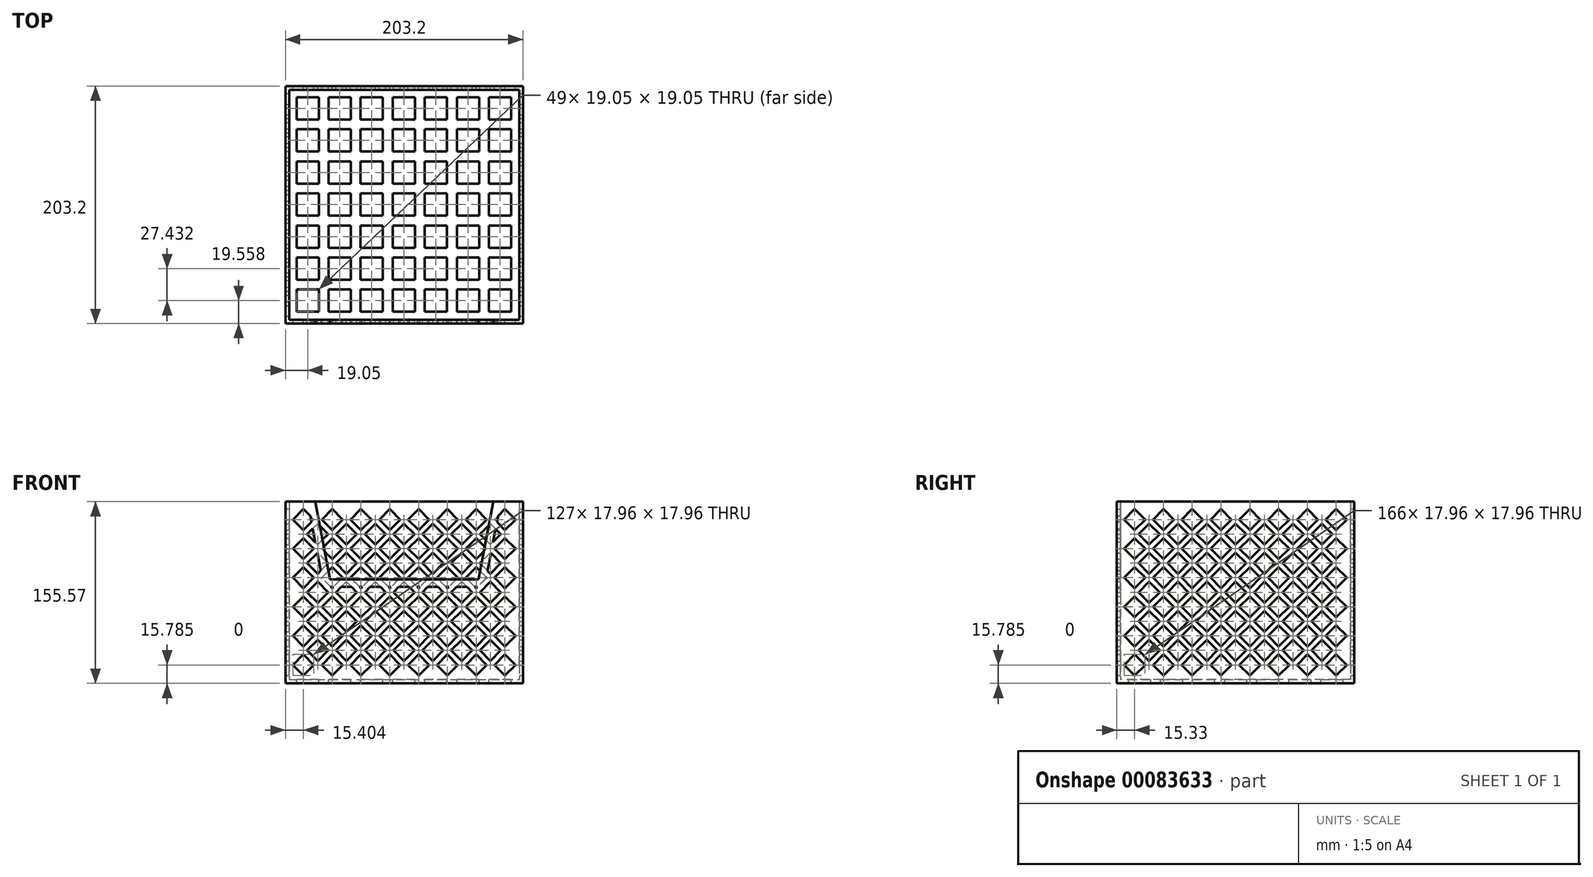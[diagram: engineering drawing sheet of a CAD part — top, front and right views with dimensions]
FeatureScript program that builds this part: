
annotation { "Feature Type Name" : "Feature", "Feature Type Description" : "" }
export const myFeature = defineFeature(function(context is Context, id is Id, definition is map)
    precondition{}
    {
        {
            var Q0;
            Q0=qCreatedBy(makeId("Top.planeOp"),FACE);
            var sketch = newSketch(context, id + "F0", { "sketchPlane" : qUnion([Q0])});
            skLineSegment(sketch, "E0.bottom", {"start": v(-101.6, 101.6) * mm, "end": v(101.6, 101.6) * mm});
            skLineSegment(sketch, "E0.top", {"start": v(-101.6, -101.6) * mm, "end": v(101.6, -101.6) * mm});
            skLineSegment(sketch, "E0.left", {"start": v(-101.6, 101.6) * mm, "end": v(-101.6, -101.6) * mm});
            skLineSegment(sketch, "E0.right", {"start": v(101.6, 101.6) * mm, "end": v(101.6, -101.6) * mm});
            skPoint(sketch, "E0.middle", {"position": v(0, 0) * mm});
            skSolve(sketch);
        }
        {
            var Q0;
            Q0=qSketchRegion(id+"F0",true);
            extrude(context, id + "F1", {"entities" : qUnion([Q0]), "depth" : 3.17 * mm});
        }
        {
            var Q0;
            Q0=makeQuery(id+"F1.opExtrude","CAP_FACE",FACE,{"disambiguationData":[OSD([sQuery(id+"F0.wireOp",EDGE,"E0.bottom"),sQuery(id+"F0.wireOp",EDGE,"E0.top"),sQuery(id+"F0.wireOp",EDGE,"E0.left"),sQuery(id+"F0.wireOp",EDGE,"E0.right")])],"isStart":false});
            var sketch = newSketch(context, id + "F2", { "sketchPlane" : qUnion([Q0])});
            skLineSegment(sketch, "E1.bottom", {"start": v(-101.6, 101.6) * mm, "end": v(101.6, 101.6) * mm});
            skLineSegment(sketch, "E1.top", {"start": v(-101.6, -101.6) * mm, "end": v(101.6, -101.6) * mm});
            skLineSegment(sketch, "E1.left", {"start": v(-101.6, 101.6) * mm, "end": v(-101.6, -101.6) * mm});
            skLineSegment(sketch, "E1.right", {"start": v(101.6, 101.6) * mm, "end": v(101.6, -101.6) * mm});
            skPoint(sketch, "E1.middle", {"position": v(0, 0) * mm});
            skLineSegment(sketch, "E2.bottom", {"start": v(-98.42, 98.43) * mm, "end": v(98.42, 98.43) * mm});
            skLineSegment(sketch, "E2.top", {"start": v(-98.42, -98.43) * mm, "end": v(98.42, -98.43) * mm});
            skLineSegment(sketch, "E2.left", {"start": v(-98.42, 98.43) * mm, "end": v(-98.42, -98.43) * mm});
            skLineSegment(sketch, "E2.right", {"start": v(98.42, 98.43) * mm, "end": v(98.42, -98.43) * mm});
            skSolve(sketch);
        }
        {
            var Q0;
            Q0=qSketchRegion(id+"F2",true);
            extrude(context, id + "F3", {"entities" : qUnion([Q0]), "operationType" : NewBodyOperationType.ADD, "depth" : 152.4 * mm});
        }
        {
            var Q0;
            Q0=makeQuery(id+"F3.boolean.opBoolean","MERGE",FACE,{"derivedFrom":[makeQuery(id+"F1.opExtrude","SWEPT_FACE",FACE,{"disambiguationData":[OSD([sQuery(id+"F0.wireOp",EDGE,"E0.top")])]}),makeQuery(id+"F3.opExtrude","SWEPT_FACE",FACE,{"disambiguationData":[OSD([sQuery(id+"F2.wireOp",EDGE,"E1.top")])]})]});
            var sketch = newSketch(context, id + "F4", { "sketchPlane" : qUnion([Q0])});
            skLineSegment(sketch, "E3", {"start": v(0, 155.58) * mm, "end": v(0, 88.9) * mm, "construction": true});
            skLineSegment(sketch, "E4", {"start": v(0, 88.9) * mm, "end": v(-63.5, 88.9) * mm});
            skLineSegment(sketch, "E5", {"start": v(-63.5, 88.9) * mm, "end": v(-76.2, 155.58) * mm});
            skLineSegment(sketch, "E6", {"start": v(-76.2, 155.58) * mm, "end": v(0, 155.58) * mm});
            skLineSegment(sketch, "E7.MirrorCS", {"start": v(0, 88.9) * mm, "end": v(63.5, 88.9) * mm});
            skLineSegment(sketch, "E8.MirrorCS", {"start": v(76.2, 155.58) * mm, "end": v(0, 155.58) * mm});
            skLineSegment(sketch, "E9.MirrorCS", {"start": v(63.5, 88.9) * mm, "end": v(76.2, 155.58) * mm});
            skSolve(sketch);
        }
        {
            var Q0;
            Q0=qSketchRegion(id+"F4",true);
            extrude(context, id + "F5", {"entities" : qUnion([Q0]), "operationType" : NewBodyOperationType.REMOVE, "endBound" : BoundingType.UP_TO_NEXT, "oppositeDirection" : true, "depth" : 25.4 * mm});
        }
        {
            var Q0;
            Q0=makeQuery(id+"F3.boolean.opBoolean","MERGE",FACE,{"derivedFrom":[makeQuery(id+"F1.opExtrude","SWEPT_FACE",FACE,{"disambiguationData":[OSD([sQuery(id+"F0.wireOp",EDGE,"E0.right")])]}),makeQuery(id+"F3.opExtrude","SWEPT_FACE",FACE,{"disambiguationData":[OSD([sQuery(id+"F2.wireOp",EDGE,"E1.right")])]})]});
            var sketch = newSketch(context, id + "F6", { "sketchPlane" : qUnion([Q0])});
            skLineSegment(sketch, "E10", {"start": v(-86.27, 149.23) * mm, "end": v(-95.25, 140.24) * mm});
            skLineSegment(sketch, "E11", {"start": v(-95.25, 140.24) * mm, "end": v(-86.27, 131.26) * mm});
            skLineSegment(sketch, "E12", {"start": v(-86.27, 131.26) * mm, "end": v(-77.29, 140.24) * mm});
            skLineSegment(sketch, "E13", {"start": v(-77.29, 140.24) * mm, "end": v(-86.27, 149.23) * mm});
            skLineSegment(sketch, "E14", {"start": v(-86.27, 131.26) * mm, "end": v(-63.2, 131.26) * mm, "construction": true});
            skLineSegment(sketch, "E15.0.1.0", {"start": v(-95.25, 115.35) * mm, "end": v(-86.27, 106.37) * mm});
            skLineSegment(sketch, "E15.0.1.1", {"start": v(-86.27, 106.37) * mm, "end": v(-77.29, 115.35) * mm});
            skLineSegment(sketch, "E15.0.1.2", {"start": v(-77.29, 115.35) * mm, "end": v(-86.27, 124.33) * mm});
            skLineSegment(sketch, "E15.0.1.3", {"start": v(-86.27, 124.33) * mm, "end": v(-95.25, 115.35) * mm});
            skLineSegment(sketch, "E15.0.2.0", {"start": v(-95.25, 90.46) * mm, "end": v(-86.27, 81.48) * mm});
            skLineSegment(sketch, "E15.0.2.1", {"start": v(-86.27, 81.48) * mm, "end": v(-77.29, 90.46) * mm});
            skLineSegment(sketch, "E15.0.2.2", {"start": v(-77.29, 90.46) * mm, "end": v(-86.27, 99.44) * mm});
            skLineSegment(sketch, "E15.0.2.3", {"start": v(-86.27, 99.44) * mm, "end": v(-95.25, 90.46) * mm});
            skLineSegment(sketch, "E15.0.3.0", {"start": v(-95.25, 65.57) * mm, "end": v(-86.27, 56.59) * mm});
            skLineSegment(sketch, "E15.0.3.1", {"start": v(-86.27, 56.59) * mm, "end": v(-77.29, 65.57) * mm});
            skLineSegment(sketch, "E15.0.3.2", {"start": v(-77.29, 65.57) * mm, "end": v(-86.27, 74.55) * mm});
            skLineSegment(sketch, "E15.0.3.3", {"start": v(-86.27, 74.55) * mm, "end": v(-95.25, 65.57) * mm});
            skLineSegment(sketch, "E15.0.4.0", {"start": v(-95.25, 40.68) * mm, "end": v(-86.27, 31.7) * mm});
            skLineSegment(sketch, "E15.0.4.1", {"start": v(-86.27, 31.7) * mm, "end": v(-77.29, 40.68) * mm});
            skLineSegment(sketch, "E15.0.4.2", {"start": v(-77.29, 40.68) * mm, "end": v(-86.27, 49.66) * mm});
            skLineSegment(sketch, "E15.0.4.3", {"start": v(-86.27, 49.66) * mm, "end": v(-95.25, 40.68) * mm});
            skLineSegment(sketch, "E15.0.5.0", {"start": v(-95.25, 15.78) * mm, "end": v(-86.27, 6.8) * mm});
            skLineSegment(sketch, "E15.0.5.1", {"start": v(-86.27, 6.8) * mm, "end": v(-77.29, 15.78) * mm});
            skLineSegment(sketch, "E15.0.5.2", {"start": v(-77.29, 15.78) * mm, "end": v(-86.27, 24.77) * mm});
            skLineSegment(sketch, "E15.0.5.3", {"start": v(-86.27, 24.77) * mm, "end": v(-95.25, 15.78) * mm});
            skLineSegment(sketch, "E15.1.0.0", {"start": v(-70.61, 140.24) * mm, "end": v(-61.63, 131.26) * mm});
            skLineSegment(sketch, "E15.1.0.1", {"start": v(-61.63, 131.26) * mm, "end": v(-52.65, 140.24) * mm});
            skLineSegment(sketch, "E15.1.0.2", {"start": v(-52.65, 140.24) * mm, "end": v(-61.63, 149.23) * mm});
            skLineSegment(sketch, "E15.1.0.3", {"start": v(-61.63, 149.23) * mm, "end": v(-70.61, 140.24) * mm});
            skLineSegment(sketch, "E15.1.1.0", {"start": v(-70.61, 115.35) * mm, "end": v(-61.63, 106.37) * mm});
            skLineSegment(sketch, "E15.1.1.1", {"start": v(-61.63, 106.37) * mm, "end": v(-52.65, 115.35) * mm});
            skLineSegment(sketch, "E15.1.1.2", {"start": v(-52.65, 115.35) * mm, "end": v(-61.63, 124.33) * mm});
            skLineSegment(sketch, "E15.1.1.3", {"start": v(-61.63, 124.33) * mm, "end": v(-70.61, 115.35) * mm});
            skLineSegment(sketch, "E15.1.2.0", {"start": v(-70.61, 90.46) * mm, "end": v(-61.63, 81.48) * mm});
            skLineSegment(sketch, "E15.1.2.1", {"start": v(-61.63, 81.48) * mm, "end": v(-52.65, 90.46) * mm});
            skLineSegment(sketch, "E15.1.2.2", {"start": v(-52.65, 90.46) * mm, "end": v(-61.63, 99.44) * mm});
            skLineSegment(sketch, "E15.1.2.3", {"start": v(-61.63, 99.44) * mm, "end": v(-70.61, 90.46) * mm});
            skLineSegment(sketch, "E15.1.3.0", {"start": v(-70.61, 65.57) * mm, "end": v(-61.63, 56.59) * mm});
            skLineSegment(sketch, "E15.1.3.1", {"start": v(-61.63, 56.59) * mm, "end": v(-52.65, 65.57) * mm});
            skLineSegment(sketch, "E15.1.3.2", {"start": v(-52.65, 65.57) * mm, "end": v(-61.63, 74.55) * mm});
            skLineSegment(sketch, "E15.1.3.3", {"start": v(-61.63, 74.55) * mm, "end": v(-70.61, 65.57) * mm});
            skLineSegment(sketch, "E15.1.4.0", {"start": v(-70.61, 40.68) * mm, "end": v(-61.63, 31.7) * mm});
            skLineSegment(sketch, "E15.1.4.1", {"start": v(-61.63, 31.7) * mm, "end": v(-52.65, 40.68) * mm});
            skLineSegment(sketch, "E15.1.4.2", {"start": v(-52.65, 40.68) * mm, "end": v(-61.63, 49.66) * mm});
            skLineSegment(sketch, "E15.1.4.3", {"start": v(-61.63, 49.66) * mm, "end": v(-70.61, 40.68) * mm});
            skLineSegment(sketch, "E15.1.5.0", {"start": v(-70.61, 15.78) * mm, "end": v(-61.63, 6.8) * mm});
            skLineSegment(sketch, "E15.1.5.1", {"start": v(-61.63, 6.8) * mm, "end": v(-52.65, 15.78) * mm});
            skLineSegment(sketch, "E15.1.5.2", {"start": v(-52.65, 15.78) * mm, "end": v(-61.63, 24.77) * mm});
            skLineSegment(sketch, "E15.1.5.3", {"start": v(-61.63, 24.77) * mm, "end": v(-70.61, 15.78) * mm});
            skLineSegment(sketch, "E15.2.0.0", {"start": v(-45.97, 140.24) * mm, "end": v(-37, 131.26) * mm});
            skLineSegment(sketch, "E15.2.0.1", {"start": v(-37, 131.26) * mm, "end": v(-28.01, 140.24) * mm});
            skLineSegment(sketch, "E15.2.0.2", {"start": v(-28.01, 140.24) * mm, "end": v(-37, 149.23) * mm});
            skLineSegment(sketch, "E15.2.0.3", {"start": v(-37, 149.23) * mm, "end": v(-45.97, 140.24) * mm});
            skLineSegment(sketch, "E15.2.1.0", {"start": v(-45.97, 115.35) * mm, "end": v(-37, 106.37) * mm});
            skLineSegment(sketch, "E15.2.1.1", {"start": v(-37, 106.37) * mm, "end": v(-28.01, 115.35) * mm});
            skLineSegment(sketch, "E15.2.1.2", {"start": v(-28.01, 115.35) * mm, "end": v(-37, 124.33) * mm});
            skLineSegment(sketch, "E15.2.1.3", {"start": v(-37, 124.33) * mm, "end": v(-45.97, 115.35) * mm});
            skLineSegment(sketch, "E15.2.2.0", {"start": v(-45.97, 90.46) * mm, "end": v(-37, 81.48) * mm});
            skLineSegment(sketch, "E15.2.2.1", {"start": v(-37, 81.48) * mm, "end": v(-28.01, 90.46) * mm});
            skLineSegment(sketch, "E15.2.2.2", {"start": v(-28.01, 90.46) * mm, "end": v(-37, 99.44) * mm});
            skLineSegment(sketch, "E15.2.2.3", {"start": v(-37, 99.44) * mm, "end": v(-45.97, 90.46) * mm});
            skLineSegment(sketch, "E15.2.3.0", {"start": v(-45.97, 65.57) * mm, "end": v(-37, 56.59) * mm});
            skLineSegment(sketch, "E15.2.3.1", {"start": v(-37, 56.59) * mm, "end": v(-28.01, 65.57) * mm});
            skLineSegment(sketch, "E15.2.3.2", {"start": v(-28.01, 65.57) * mm, "end": v(-37, 74.55) * mm});
            skLineSegment(sketch, "E15.2.3.3", {"start": v(-37, 74.55) * mm, "end": v(-45.97, 65.57) * mm});
            skLineSegment(sketch, "E15.2.4.0", {"start": v(-45.97, 40.68) * mm, "end": v(-37, 31.7) * mm});
            skLineSegment(sketch, "E15.2.4.1", {"start": v(-37, 31.7) * mm, "end": v(-28.01, 40.68) * mm});
            skLineSegment(sketch, "E15.2.4.2", {"start": v(-28.01, 40.68) * mm, "end": v(-37, 49.66) * mm});
            skLineSegment(sketch, "E15.2.4.3", {"start": v(-37, 49.66) * mm, "end": v(-45.97, 40.68) * mm});
            skLineSegment(sketch, "E15.2.5.0", {"start": v(-45.97, 15.78) * mm, "end": v(-37, 6.8) * mm});
            skLineSegment(sketch, "E15.2.5.1", {"start": v(-37, 6.8) * mm, "end": v(-28.01, 15.78) * mm});
            skLineSegment(sketch, "E15.2.5.2", {"start": v(-28.01, 15.78) * mm, "end": v(-37, 24.77) * mm});
            skLineSegment(sketch, "E15.2.5.3", {"start": v(-37, 24.77) * mm, "end": v(-45.97, 15.78) * mm});
            skLineSegment(sketch, "E15.3.0.0", {"start": v(-21.34, 140.24) * mm, "end": v(-12.36, 131.26) * mm});
            skLineSegment(sketch, "E15.3.0.1", {"start": v(-12.36, 131.26) * mm, "end": v(-3.38, 140.24) * mm});
            skLineSegment(sketch, "E15.3.0.2", {"start": v(-3.38, 140.24) * mm, "end": v(-12.36, 149.23) * mm});
            skLineSegment(sketch, "E15.3.0.3", {"start": v(-12.36, 149.23) * mm, "end": v(-21.34, 140.24) * mm});
            skLineSegment(sketch, "E15.3.1.0", {"start": v(-21.34, 115.35) * mm, "end": v(-12.36, 106.37) * mm});
            skLineSegment(sketch, "E15.3.1.1", {"start": v(-12.36, 106.37) * mm, "end": v(-3.38, 115.35) * mm});
            skLineSegment(sketch, "E15.3.1.2", {"start": v(-3.38, 115.35) * mm, "end": v(-12.36, 124.33) * mm});
            skLineSegment(sketch, "E15.3.1.3", {"start": v(-12.36, 124.33) * mm, "end": v(-21.34, 115.35) * mm});
            skLineSegment(sketch, "E15.3.2.0", {"start": v(-21.34, 90.46) * mm, "end": v(-12.36, 81.48) * mm});
            skLineSegment(sketch, "E15.3.2.1", {"start": v(-12.36, 81.48) * mm, "end": v(-3.38, 90.46) * mm});
            skLineSegment(sketch, "E15.3.2.2", {"start": v(-3.38, 90.46) * mm, "end": v(-12.36, 99.44) * mm});
            skLineSegment(sketch, "E15.3.2.3", {"start": v(-12.36, 99.44) * mm, "end": v(-21.34, 90.46) * mm});
            skLineSegment(sketch, "E15.3.3.0", {"start": v(-21.34, 65.57) * mm, "end": v(-12.36, 56.59) * mm});
            skLineSegment(sketch, "E15.3.3.1", {"start": v(-12.36, 56.59) * mm, "end": v(-3.38, 65.57) * mm});
            skLineSegment(sketch, "E15.3.3.2", {"start": v(-3.38, 65.57) * mm, "end": v(-12.36, 74.55) * mm});
            skLineSegment(sketch, "E15.3.3.3", {"start": v(-12.36, 74.55) * mm, "end": v(-21.34, 65.57) * mm});
            skLineSegment(sketch, "E15.3.4.0", {"start": v(-21.34, 40.68) * mm, "end": v(-12.36, 31.7) * mm});
            skLineSegment(sketch, "E15.3.4.1", {"start": v(-12.36, 31.7) * mm, "end": v(-3.38, 40.68) * mm});
            skLineSegment(sketch, "E15.3.4.2", {"start": v(-3.38, 40.68) * mm, "end": v(-12.36, 49.66) * mm});
            skLineSegment(sketch, "E15.3.4.3", {"start": v(-12.36, 49.66) * mm, "end": v(-21.34, 40.68) * mm});
            skLineSegment(sketch, "E15.3.5.0", {"start": v(-21.34, 15.78) * mm, "end": v(-12.36, 6.8) * mm});
            skLineSegment(sketch, "E15.3.5.1", {"start": v(-12.36, 6.8) * mm, "end": v(-3.38, 15.78) * mm});
            skLineSegment(sketch, "E15.3.5.2", {"start": v(-3.38, 15.78) * mm, "end": v(-12.36, 24.77) * mm});
            skLineSegment(sketch, "E15.3.5.3", {"start": v(-12.36, 24.77) * mm, "end": v(-21.34, 15.78) * mm});
            skLineSegment(sketch, "E15.4.0.0", {"start": v(3.3, 140.24) * mm, "end": v(12.28, 131.26) * mm});
            skLineSegment(sketch, "E15.4.0.1", {"start": v(12.28, 131.26) * mm, "end": v(21.26, 140.24) * mm});
            skLineSegment(sketch, "E15.4.0.2", {"start": v(21.26, 140.24) * mm, "end": v(12.28, 149.23) * mm});
            skLineSegment(sketch, "E15.4.0.3", {"start": v(12.28, 149.23) * mm, "end": v(3.3, 140.24) * mm});
            skLineSegment(sketch, "E15.4.1.0", {"start": v(3.3, 115.35) * mm, "end": v(12.28, 106.37) * mm});
            skLineSegment(sketch, "E15.4.1.1", {"start": v(12.28, 106.37) * mm, "end": v(21.26, 115.35) * mm});
            skLineSegment(sketch, "E15.4.1.2", {"start": v(21.26, 115.35) * mm, "end": v(12.28, 124.33) * mm});
            skLineSegment(sketch, "E15.4.1.3", {"start": v(12.28, 124.33) * mm, "end": v(3.3, 115.35) * mm});
            skLineSegment(sketch, "E15.4.2.0", {"start": v(3.3, 90.46) * mm, "end": v(12.28, 81.48) * mm});
            skLineSegment(sketch, "E15.4.2.1", {"start": v(12.28, 81.48) * mm, "end": v(21.26, 90.46) * mm});
            skLineSegment(sketch, "E15.4.2.2", {"start": v(21.26, 90.46) * mm, "end": v(12.28, 99.44) * mm});
            skLineSegment(sketch, "E15.4.2.3", {"start": v(12.28, 99.44) * mm, "end": v(3.3, 90.46) * mm});
            skLineSegment(sketch, "E15.4.3.0", {"start": v(3.3, 65.57) * mm, "end": v(12.28, 56.59) * mm});
            skLineSegment(sketch, "E15.4.3.1", {"start": v(12.28, 56.59) * mm, "end": v(21.26, 65.57) * mm});
            skLineSegment(sketch, "E15.4.3.2", {"start": v(21.26, 65.57) * mm, "end": v(12.28, 74.55) * mm});
            skLineSegment(sketch, "E15.4.3.3", {"start": v(12.28, 74.55) * mm, "end": v(3.3, 65.57) * mm});
            skLineSegment(sketch, "E15.4.4.0", {"start": v(3.3, 40.68) * mm, "end": v(12.28, 31.7) * mm});
            skLineSegment(sketch, "E15.4.4.1", {"start": v(12.28, 31.7) * mm, "end": v(21.26, 40.68) * mm});
            skLineSegment(sketch, "E15.4.4.2", {"start": v(21.26, 40.68) * mm, "end": v(12.28, 49.66) * mm});
            skLineSegment(sketch, "E15.4.4.3", {"start": v(12.28, 49.66) * mm, "end": v(3.3, 40.68) * mm});
            skLineSegment(sketch, "E15.4.5.0", {"start": v(3.3, 15.78) * mm, "end": v(12.28, 6.8) * mm});
            skLineSegment(sketch, "E15.4.5.1", {"start": v(12.28, 6.8) * mm, "end": v(21.26, 15.78) * mm});
            skLineSegment(sketch, "E15.4.5.2", {"start": v(21.26, 15.78) * mm, "end": v(12.28, 24.77) * mm});
            skLineSegment(sketch, "E15.4.5.3", {"start": v(12.28, 24.77) * mm, "end": v(3.3, 15.78) * mm});
            skLineSegment(sketch, "E15.5.0.0", {"start": v(27.94, 140.24) * mm, "end": v(36.92, 131.26) * mm});
            skLineSegment(sketch, "E15.5.0.1", {"start": v(36.92, 131.26) * mm, "end": v(45.9, 140.24) * mm});
            skLineSegment(sketch, "E15.5.0.2", {"start": v(45.9, 140.24) * mm, "end": v(36.92, 149.23) * mm});
            skLineSegment(sketch, "E15.5.0.3", {"start": v(36.92, 149.23) * mm, "end": v(27.94, 140.24) * mm});
            skLineSegment(sketch, "E15.5.1.0", {"start": v(27.94, 115.35) * mm, "end": v(36.92, 106.37) * mm});
            skLineSegment(sketch, "E15.5.1.1", {"start": v(36.92, 106.37) * mm, "end": v(45.9, 115.35) * mm});
            skLineSegment(sketch, "E15.5.1.2", {"start": v(45.9, 115.35) * mm, "end": v(36.92, 124.33) * mm});
            skLineSegment(sketch, "E15.5.1.3", {"start": v(36.92, 124.33) * mm, "end": v(27.94, 115.35) * mm});
            skLineSegment(sketch, "E15.5.2.0", {"start": v(27.94, 90.46) * mm, "end": v(36.92, 81.48) * mm});
            skLineSegment(sketch, "E15.5.2.1", {"start": v(36.92, 81.48) * mm, "end": v(45.9, 90.46) * mm});
            skLineSegment(sketch, "E15.5.2.2", {"start": v(45.9, 90.46) * mm, "end": v(36.92, 99.44) * mm});
            skLineSegment(sketch, "E15.5.2.3", {"start": v(36.92, 99.44) * mm, "end": v(27.94, 90.46) * mm});
            skLineSegment(sketch, "E15.5.3.0", {"start": v(27.94, 65.57) * mm, "end": v(36.92, 56.59) * mm});
            skLineSegment(sketch, "E15.5.3.1", {"start": v(36.92, 56.59) * mm, "end": v(45.9, 65.57) * mm});
            skLineSegment(sketch, "E15.5.3.2", {"start": v(45.9, 65.57) * mm, "end": v(36.92, 74.55) * mm});
            skLineSegment(sketch, "E15.5.3.3", {"start": v(36.92, 74.55) * mm, "end": v(27.94, 65.57) * mm});
            skLineSegment(sketch, "E15.5.4.0", {"start": v(27.94, 40.68) * mm, "end": v(36.92, 31.7) * mm});
            skLineSegment(sketch, "E15.5.4.1", {"start": v(36.92, 31.7) * mm, "end": v(45.9, 40.68) * mm});
            skLineSegment(sketch, "E15.5.4.2", {"start": v(45.9, 40.68) * mm, "end": v(36.92, 49.66) * mm});
            skLineSegment(sketch, "E15.5.4.3", {"start": v(36.92, 49.66) * mm, "end": v(27.94, 40.68) * mm});
            skLineSegment(sketch, "E15.5.5.0", {"start": v(27.94, 15.78) * mm, "end": v(36.92, 6.8) * mm});
            skLineSegment(sketch, "E15.5.5.1", {"start": v(36.92, 6.8) * mm, "end": v(45.9, 15.78) * mm});
            skLineSegment(sketch, "E15.5.5.2", {"start": v(45.9, 15.78) * mm, "end": v(36.92, 24.77) * mm});
            skLineSegment(sketch, "E15.5.5.3", {"start": v(36.92, 24.77) * mm, "end": v(27.94, 15.78) * mm});
            skLineSegment(sketch, "E15.6.0.0", {"start": v(52.58, 140.24) * mm, "end": v(61.56, 131.26) * mm});
            skLineSegment(sketch, "E15.6.0.1", {"start": v(61.56, 131.26) * mm, "end": v(70.54, 140.24) * mm});
            skLineSegment(sketch, "E15.6.0.2", {"start": v(70.54, 140.24) * mm, "end": v(61.56, 149.23) * mm});
            skLineSegment(sketch, "E15.6.0.3", {"start": v(61.56, 149.23) * mm, "end": v(52.58, 140.24) * mm});
            skLineSegment(sketch, "E15.6.1.0", {"start": v(52.58, 115.35) * mm, "end": v(61.56, 106.37) * mm});
            skLineSegment(sketch, "E15.6.1.1", {"start": v(61.56, 106.37) * mm, "end": v(70.54, 115.35) * mm});
            skLineSegment(sketch, "E15.6.1.2", {"start": v(70.54, 115.35) * mm, "end": v(61.56, 124.33) * mm});
            skLineSegment(sketch, "E15.6.1.3", {"start": v(61.56, 124.33) * mm, "end": v(52.58, 115.35) * mm});
            skLineSegment(sketch, "E15.6.2.0", {"start": v(52.58, 90.46) * mm, "end": v(61.56, 81.48) * mm});
            skLineSegment(sketch, "E15.6.2.1", {"start": v(61.56, 81.48) * mm, "end": v(70.54, 90.46) * mm});
            skLineSegment(sketch, "E15.6.2.2", {"start": v(70.54, 90.46) * mm, "end": v(61.56, 99.44) * mm});
            skLineSegment(sketch, "E15.6.2.3", {"start": v(61.56, 99.44) * mm, "end": v(52.58, 90.46) * mm});
            skLineSegment(sketch, "E15.6.3.0", {"start": v(52.58, 65.57) * mm, "end": v(61.56, 56.59) * mm});
            skLineSegment(sketch, "E15.6.3.1", {"start": v(61.56, 56.59) * mm, "end": v(70.54, 65.57) * mm});
            skLineSegment(sketch, "E15.6.3.2", {"start": v(70.54, 65.57) * mm, "end": v(61.56, 74.55) * mm});
            skLineSegment(sketch, "E15.6.3.3", {"start": v(61.56, 74.55) * mm, "end": v(52.58, 65.57) * mm});
            skLineSegment(sketch, "E15.6.4.0", {"start": v(52.58, 40.68) * mm, "end": v(61.56, 31.7) * mm});
            skLineSegment(sketch, "E15.6.4.1", {"start": v(61.56, 31.7) * mm, "end": v(70.54, 40.68) * mm});
            skLineSegment(sketch, "E15.6.4.2", {"start": v(70.54, 40.68) * mm, "end": v(61.56, 49.66) * mm});
            skLineSegment(sketch, "E15.6.4.3", {"start": v(61.56, 49.66) * mm, "end": v(52.58, 40.68) * mm});
            skLineSegment(sketch, "E15.6.5.0", {"start": v(52.58, 15.78) * mm, "end": v(61.56, 6.8) * mm});
            skLineSegment(sketch, "E15.6.5.1", {"start": v(61.56, 6.8) * mm, "end": v(70.54, 15.78) * mm});
            skLineSegment(sketch, "E15.6.5.2", {"start": v(70.54, 15.78) * mm, "end": v(61.56, 24.77) * mm});
            skLineSegment(sketch, "E15.6.5.3", {"start": v(61.56, 24.77) * mm, "end": v(52.58, 15.78) * mm});
            skLineSegment(sketch, "E15.7.0.0", {"start": v(77.22, 140.24) * mm, "end": v(86.2, 131.26) * mm});
            skLineSegment(sketch, "E15.7.0.1", {"start": v(86.2, 131.26) * mm, "end": v(95.18, 140.24) * mm});
            skLineSegment(sketch, "E15.7.0.2", {"start": v(95.18, 140.24) * mm, "end": v(86.2, 149.23) * mm});
            skLineSegment(sketch, "E15.7.0.3", {"start": v(86.2, 149.23) * mm, "end": v(77.22, 140.24) * mm});
            skLineSegment(sketch, "E15.7.1.0", {"start": v(77.22, 115.35) * mm, "end": v(86.2, 106.37) * mm});
            skLineSegment(sketch, "E15.7.1.1", {"start": v(86.2, 106.37) * mm, "end": v(95.18, 115.35) * mm});
            skLineSegment(sketch, "E15.7.1.2", {"start": v(95.18, 115.35) * mm, "end": v(86.2, 124.33) * mm});
            skLineSegment(sketch, "E15.7.1.3", {"start": v(86.2, 124.33) * mm, "end": v(77.22, 115.35) * mm});
            skLineSegment(sketch, "E15.7.2.0", {"start": v(77.22, 90.46) * mm, "end": v(86.2, 81.48) * mm});
            skLineSegment(sketch, "E15.7.2.1", {"start": v(86.2, 81.48) * mm, "end": v(95.18, 90.46) * mm});
            skLineSegment(sketch, "E15.7.2.2", {"start": v(95.18, 90.46) * mm, "end": v(86.2, 99.44) * mm});
            skLineSegment(sketch, "E15.7.2.3", {"start": v(86.2, 99.44) * mm, "end": v(77.22, 90.46) * mm});
            skLineSegment(sketch, "E15.7.3.0", {"start": v(77.22, 65.57) * mm, "end": v(86.2, 56.59) * mm});
            skLineSegment(sketch, "E15.7.3.1", {"start": v(86.2, 56.59) * mm, "end": v(95.18, 65.57) * mm});
            skLineSegment(sketch, "E15.7.3.2", {"start": v(95.18, 65.57) * mm, "end": v(86.2, 74.55) * mm});
            skLineSegment(sketch, "E15.7.3.3", {"start": v(86.2, 74.55) * mm, "end": v(77.22, 65.57) * mm});
            skLineSegment(sketch, "E15.7.4.0", {"start": v(77.22, 40.68) * mm, "end": v(86.2, 31.7) * mm});
            skLineSegment(sketch, "E15.7.4.1", {"start": v(86.2, 31.7) * mm, "end": v(95.18, 40.68) * mm});
            skLineSegment(sketch, "E15.7.4.2", {"start": v(95.18, 40.68) * mm, "end": v(86.2, 49.66) * mm});
            skLineSegment(sketch, "E15.7.4.3", {"start": v(86.2, 49.66) * mm, "end": v(77.22, 40.68) * mm});
            skLineSegment(sketch, "E15.7.5.0", {"start": v(77.22, 15.78) * mm, "end": v(86.2, 6.8) * mm});
            skLineSegment(sketch, "E15.7.5.1", {"start": v(86.2, 6.8) * mm, "end": v(95.18, 15.78) * mm});
            skLineSegment(sketch, "E15.7.5.2", {"start": v(95.18, 15.78) * mm, "end": v(86.2, 24.77) * mm});
            skLineSegment(sketch, "E15.7.5.3", {"start": v(86.2, 24.77) * mm, "end": v(77.22, 15.78) * mm});
            skLineSegment(sketch, "E15.direction1", {"start": v(-86.27, 131.26) * mm, "end": v(-61.63, 131.26) * mm, "construction": true});
            skLineSegment(sketch, "E15.direction2", {"start": v(-86.27, 131.26) * mm, "end": v(-86.27, 106.37) * mm, "construction": true});
            skSolve(sketch);
        }
        {
            var Q0;
            Q0=qSketchRegion(id+"F6",true);
            extrude(context, id + "F7", {"entities" : qUnion([Q0]), "operationType" : NewBodyOperationType.REMOVE, "endBound" : BoundingType.THROUGH_ALL, "oppositeDirection" : true, "depth" : 25.4 * mm});
        }
        {
            var Q0;
            Q0=makeQuery(id+"F3.boolean.opBoolean","MERGE",FACE,{"derivedFrom":[makeQuery(id+"F1.opExtrude","SWEPT_FACE",FACE,{"disambiguationData":[OSD([sQuery(id+"F0.wireOp",EDGE,"E0.right")])]}),makeQuery(id+"F3.opExtrude","SWEPT_FACE",FACE,{"disambiguationData":[OSD([sQuery(id+"F2.wireOp",EDGE,"E1.right")])]})]});
            var sketch = newSketch(context, id + "F8", { "sketchPlane" : qUnion([Q0])});
            skLineSegment(sketch, "E16", {"start": v(-73.82, 136.78) * mm, "end": v(-82.8, 127.8) * mm});
            skLineSegment(sketch, "E17", {"start": v(-82.8, 127.8) * mm, "end": v(-73.82, 118.82) * mm});
            skLineSegment(sketch, "E18", {"start": v(-73.82, 118.82) * mm, "end": v(-64.84, 127.8) * mm});
            skLineSegment(sketch, "E19", {"start": v(-64.84, 127.8) * mm, "end": v(-73.82, 136.78) * mm});
            skLineSegment(sketch, "E20.0.1.0", {"start": v(-64.84, 102.9) * mm, "end": v(-73.82, 111.89) * mm});
            skLineSegment(sketch, "E20.0.1.1", {"start": v(-73.82, 93.93) * mm, "end": v(-64.84, 102.9) * mm});
            skLineSegment(sketch, "E20.0.1.2", {"start": v(-82.8, 102.9) * mm, "end": v(-73.82, 93.93) * mm});
            skLineSegment(sketch, "E20.0.1.3", {"start": v(-73.82, 111.89) * mm, "end": v(-82.8, 102.9) * mm});
            skLineSegment(sketch, "E20.0.2.0", {"start": v(-64.84, 78.01) * mm, "end": v(-73.82, 87) * mm});
            skLineSegment(sketch, "E20.0.2.1", {"start": v(-73.82, 69.03) * mm, "end": v(-64.84, 78.01) * mm});
            skLineSegment(sketch, "E20.0.2.2", {"start": v(-82.8, 78.01) * mm, "end": v(-73.82, 69.03) * mm});
            skLineSegment(sketch, "E20.0.2.3", {"start": v(-73.82, 87) * mm, "end": v(-82.8, 78.01) * mm});
            skLineSegment(sketch, "E20.0.3.0", {"start": v(-64.84, 53.12) * mm, "end": v(-73.82, 62.1) * mm});
            skLineSegment(sketch, "E20.0.3.1", {"start": v(-73.82, 44.14) * mm, "end": v(-64.84, 53.12) * mm});
            skLineSegment(sketch, "E20.0.3.2", {"start": v(-82.8, 53.12) * mm, "end": v(-73.82, 44.14) * mm});
            skLineSegment(sketch, "E20.0.3.3", {"start": v(-73.82, 62.1) * mm, "end": v(-82.8, 53.12) * mm});
            skLineSegment(sketch, "E20.0.4.0", {"start": v(-64.84, 28.23) * mm, "end": v(-73.82, 37.21) * mm});
            skLineSegment(sketch, "E20.0.4.1", {"start": v(-73.82, 19.25) * mm, "end": v(-64.84, 28.23) * mm});
            skLineSegment(sketch, "E20.0.4.2", {"start": v(-82.8, 28.23) * mm, "end": v(-73.82, 19.25) * mm});
            skLineSegment(sketch, "E20.0.4.3", {"start": v(-73.82, 37.21) * mm, "end": v(-82.8, 28.23) * mm});
            skLineSegment(sketch, "E20.1.0.0", {"start": v(-40.2, 127.8) * mm, "end": v(-49.19, 136.78) * mm});
            skLineSegment(sketch, "E20.1.0.1", {"start": v(-49.19, 118.82) * mm, "end": v(-40.2, 127.8) * mm});
            skLineSegment(sketch, "E20.1.0.2", {"start": v(-58.17, 127.8) * mm, "end": v(-49.19, 118.82) * mm});
            skLineSegment(sketch, "E20.1.0.3", {"start": v(-49.19, 136.78) * mm, "end": v(-58.17, 127.8) * mm});
            skLineSegment(sketch, "E20.1.1.0", {"start": v(-40.2, 102.9) * mm, "end": v(-49.19, 111.89) * mm});
            skLineSegment(sketch, "E20.1.1.1", {"start": v(-49.19, 93.93) * mm, "end": v(-40.2, 102.9) * mm});
            skLineSegment(sketch, "E20.1.1.2", {"start": v(-58.17, 102.9) * mm, "end": v(-49.19, 93.93) * mm});
            skLineSegment(sketch, "E20.1.1.3", {"start": v(-49.19, 111.89) * mm, "end": v(-58.17, 102.9) * mm});
            skLineSegment(sketch, "E20.1.2.0", {"start": v(-40.2, 78.01) * mm, "end": v(-49.19, 87) * mm});
            skLineSegment(sketch, "E20.1.2.1", {"start": v(-49.19, 69.03) * mm, "end": v(-40.2, 78.01) * mm});
            skLineSegment(sketch, "E20.1.2.2", {"start": v(-58.17, 78.01) * mm, "end": v(-49.19, 69.03) * mm});
            skLineSegment(sketch, "E20.1.2.3", {"start": v(-49.19, 87) * mm, "end": v(-58.17, 78.01) * mm});
            skLineSegment(sketch, "E20.1.3.0", {"start": v(-40.2, 53.12) * mm, "end": v(-49.19, 62.1) * mm});
            skLineSegment(sketch, "E20.1.3.1", {"start": v(-49.19, 44.14) * mm, "end": v(-40.2, 53.12) * mm});
            skLineSegment(sketch, "E20.1.3.2", {"start": v(-58.17, 53.12) * mm, "end": v(-49.19, 44.14) * mm});
            skLineSegment(sketch, "E20.1.3.3", {"start": v(-49.19, 62.1) * mm, "end": v(-58.17, 53.12) * mm});
            skLineSegment(sketch, "E20.1.4.0", {"start": v(-40.2, 28.23) * mm, "end": v(-49.19, 37.21) * mm});
            skLineSegment(sketch, "E20.1.4.1", {"start": v(-49.19, 19.25) * mm, "end": v(-40.2, 28.23) * mm});
            skLineSegment(sketch, "E20.1.4.2", {"start": v(-58.17, 28.23) * mm, "end": v(-49.19, 19.25) * mm});
            skLineSegment(sketch, "E20.1.4.3", {"start": v(-49.19, 37.21) * mm, "end": v(-58.17, 28.23) * mm});
            skLineSegment(sketch, "E20.2.0.0", {"start": v(-15.57, 127.8) * mm, "end": v(-24.55, 136.78) * mm});
            skLineSegment(sketch, "E20.2.0.1", {"start": v(-24.55, 118.82) * mm, "end": v(-15.57, 127.8) * mm});
            skLineSegment(sketch, "E20.2.0.2", {"start": v(-33.53, 127.8) * mm, "end": v(-24.55, 118.82) * mm});
            skLineSegment(sketch, "E20.2.0.3", {"start": v(-24.55, 136.78) * mm, "end": v(-33.53, 127.8) * mm});
            skLineSegment(sketch, "E20.2.1.0", {"start": v(-15.57, 102.9) * mm, "end": v(-24.55, 111.89) * mm});
            skLineSegment(sketch, "E20.2.1.1", {"start": v(-24.55, 93.93) * mm, "end": v(-15.57, 102.9) * mm});
            skLineSegment(sketch, "E20.2.1.2", {"start": v(-33.53, 102.9) * mm, "end": v(-24.55, 93.93) * mm});
            skLineSegment(sketch, "E20.2.1.3", {"start": v(-24.55, 111.89) * mm, "end": v(-33.53, 102.9) * mm});
            skLineSegment(sketch, "E20.2.2.0", {"start": v(-15.57, 78.01) * mm, "end": v(-24.55, 87) * mm});
            skLineSegment(sketch, "E20.2.2.1", {"start": v(-24.55, 69.03) * mm, "end": v(-15.57, 78.01) * mm});
            skLineSegment(sketch, "E20.2.2.2", {"start": v(-33.53, 78.01) * mm, "end": v(-24.55, 69.03) * mm});
            skLineSegment(sketch, "E20.2.2.3", {"start": v(-24.55, 87) * mm, "end": v(-33.53, 78.01) * mm});
            skLineSegment(sketch, "E20.2.3.0", {"start": v(-15.57, 53.12) * mm, "end": v(-24.55, 62.1) * mm});
            skLineSegment(sketch, "E20.2.3.1", {"start": v(-24.55, 44.14) * mm, "end": v(-15.57, 53.12) * mm});
            skLineSegment(sketch, "E20.2.3.2", {"start": v(-33.53, 53.12) * mm, "end": v(-24.55, 44.14) * mm});
            skLineSegment(sketch, "E20.2.3.3", {"start": v(-24.55, 62.1) * mm, "end": v(-33.53, 53.12) * mm});
            skLineSegment(sketch, "E20.2.4.0", {"start": v(-15.57, 28.23) * mm, "end": v(-24.55, 37.21) * mm});
            skLineSegment(sketch, "E20.2.4.1", {"start": v(-24.55, 19.25) * mm, "end": v(-15.57, 28.23) * mm});
            skLineSegment(sketch, "E20.2.4.2", {"start": v(-33.53, 28.23) * mm, "end": v(-24.55, 19.25) * mm});
            skLineSegment(sketch, "E20.2.4.3", {"start": v(-24.55, 37.21) * mm, "end": v(-33.53, 28.23) * mm});
            skLineSegment(sketch, "E20.3.0.0", {"start": v(9.07, 127.8) * mm, "end": v(0.1, 136.78) * mm});
            skLineSegment(sketch, "E20.3.0.1", {"start": v(0.1, 118.82) * mm, "end": v(9.07, 127.8) * mm});
            skLineSegment(sketch, "E20.3.0.2", {"start": v(-8.9, 127.8) * mm, "end": v(0.1, 118.82) * mm});
            skLineSegment(sketch, "E20.3.0.3", {"start": v(0.1, 136.78) * mm, "end": v(-8.9, 127.8) * mm});
            skLineSegment(sketch, "E20.3.1.0", {"start": v(9.07, 102.9) * mm, "end": v(0.1, 111.89) * mm});
            skLineSegment(sketch, "E20.3.1.1", {"start": v(0.1, 93.93) * mm, "end": v(9.07, 102.9) * mm});
            skLineSegment(sketch, "E20.3.1.2", {"start": v(-8.9, 102.9) * mm, "end": v(0.1, 93.93) * mm});
            skLineSegment(sketch, "E20.3.1.3", {"start": v(0.1, 111.89) * mm, "end": v(-8.9, 102.9) * mm});
            skLineSegment(sketch, "E20.3.2.0", {"start": v(9.07, 78.01) * mm, "end": v(0.1, 87) * mm});
            skLineSegment(sketch, "E20.3.2.1", {"start": v(0.1, 69.03) * mm, "end": v(9.07, 78.01) * mm});
            skLineSegment(sketch, "E20.3.2.2", {"start": v(-8.9, 78.01) * mm, "end": v(0.1, 69.03) * mm});
            skLineSegment(sketch, "E20.3.2.3", {"start": v(0.1, 87) * mm, "end": v(-8.9, 78.01) * mm});
            skLineSegment(sketch, "E20.3.3.0", {"start": v(9.07, 53.12) * mm, "end": v(0.1, 62.1) * mm});
            skLineSegment(sketch, "E20.3.3.1", {"start": v(0.1, 44.14) * mm, "end": v(9.07, 53.12) * mm});
            skLineSegment(sketch, "E20.3.3.2", {"start": v(-8.9, 53.12) * mm, "end": v(0.1, 44.14) * mm});
            skLineSegment(sketch, "E20.3.3.3", {"start": v(0.1, 62.1) * mm, "end": v(-8.9, 53.12) * mm});
            skLineSegment(sketch, "E20.3.4.0", {"start": v(9.07, 28.23) * mm, "end": v(0.1, 37.21) * mm});
            skLineSegment(sketch, "E20.3.4.1", {"start": v(0.1, 19.25) * mm, "end": v(9.07, 28.23) * mm});
            skLineSegment(sketch, "E20.3.4.2", {"start": v(-8.9, 28.23) * mm, "end": v(0.1, 19.25) * mm});
            skLineSegment(sketch, "E20.3.4.3", {"start": v(0.1, 37.21) * mm, "end": v(-8.9, 28.23) * mm});
            skLineSegment(sketch, "E20.4.0.0", {"start": v(33.7, 127.8) * mm, "end": v(24.73, 136.78) * mm});
            skLineSegment(sketch, "E20.4.0.1", {"start": v(24.73, 118.82) * mm, "end": v(33.7, 127.8) * mm});
            skLineSegment(sketch, "E20.4.0.2", {"start": v(15.75, 127.8) * mm, "end": v(24.73, 118.82) * mm});
            skLineSegment(sketch, "E20.4.0.3", {"start": v(24.73, 136.78) * mm, "end": v(15.75, 127.8) * mm});
            skLineSegment(sketch, "E20.4.1.0", {"start": v(33.7, 102.9) * mm, "end": v(24.73, 111.89) * mm});
            skLineSegment(sketch, "E20.4.1.1", {"start": v(24.73, 93.93) * mm, "end": v(33.7, 102.9) * mm});
            skLineSegment(sketch, "E20.4.1.2", {"start": v(15.75, 102.9) * mm, "end": v(24.73, 93.93) * mm});
            skLineSegment(sketch, "E20.4.1.3", {"start": v(24.73, 111.89) * mm, "end": v(15.75, 102.9) * mm});
            skLineSegment(sketch, "E20.4.2.0", {"start": v(33.7, 78.01) * mm, "end": v(24.73, 87) * mm});
            skLineSegment(sketch, "E20.4.2.1", {"start": v(24.73, 69.03) * mm, "end": v(33.7, 78.01) * mm});
            skLineSegment(sketch, "E20.4.2.2", {"start": v(15.75, 78.01) * mm, "end": v(24.73, 69.03) * mm});
            skLineSegment(sketch, "E20.4.2.3", {"start": v(24.73, 87) * mm, "end": v(15.75, 78.01) * mm});
            skLineSegment(sketch, "E20.4.3.0", {"start": v(33.7, 53.12) * mm, "end": v(24.73, 62.1) * mm});
            skLineSegment(sketch, "E20.4.3.1", {"start": v(24.73, 44.14) * mm, "end": v(33.7, 53.12) * mm});
            skLineSegment(sketch, "E20.4.3.2", {"start": v(15.75, 53.12) * mm, "end": v(24.73, 44.14) * mm});
            skLineSegment(sketch, "E20.4.3.3", {"start": v(24.73, 62.1) * mm, "end": v(15.75, 53.12) * mm});
            skLineSegment(sketch, "E20.4.4.0", {"start": v(33.7, 28.23) * mm, "end": v(24.73, 37.21) * mm});
            skLineSegment(sketch, "E20.4.4.1", {"start": v(24.73, 19.25) * mm, "end": v(33.7, 28.23) * mm});
            skLineSegment(sketch, "E20.4.4.2", {"start": v(15.75, 28.23) * mm, "end": v(24.73, 19.25) * mm});
            skLineSegment(sketch, "E20.4.4.3", {"start": v(24.73, 37.21) * mm, "end": v(15.75, 28.23) * mm});
            skLineSegment(sketch, "E20.5.0.0", {"start": v(58.35, 127.8) * mm, "end": v(49.37, 136.78) * mm});
            skLineSegment(sketch, "E20.5.0.1", {"start": v(49.37, 118.82) * mm, "end": v(58.35, 127.8) * mm});
            skLineSegment(sketch, "E20.5.0.2", {"start": v(40.39, 127.8) * mm, "end": v(49.37, 118.82) * mm});
            skLineSegment(sketch, "E20.5.0.3", {"start": v(49.37, 136.78) * mm, "end": v(40.39, 127.8) * mm});
            skLineSegment(sketch, "E20.5.1.0", {"start": v(58.35, 102.9) * mm, "end": v(49.37, 111.89) * mm});
            skLineSegment(sketch, "E20.5.1.1", {"start": v(49.37, 93.93) * mm, "end": v(58.35, 102.9) * mm});
            skLineSegment(sketch, "E20.5.1.2", {"start": v(40.39, 102.9) * mm, "end": v(49.37, 93.93) * mm});
            skLineSegment(sketch, "E20.5.1.3", {"start": v(49.37, 111.89) * mm, "end": v(40.39, 102.9) * mm});
            skLineSegment(sketch, "E20.5.2.0", {"start": v(58.35, 78.01) * mm, "end": v(49.37, 87) * mm});
            skLineSegment(sketch, "E20.5.2.1", {"start": v(49.37, 69.03) * mm, "end": v(58.35, 78.01) * mm});
            skLineSegment(sketch, "E20.5.2.2", {"start": v(40.39, 78.01) * mm, "end": v(49.37, 69.03) * mm});
            skLineSegment(sketch, "E20.5.2.3", {"start": v(49.37, 87) * mm, "end": v(40.39, 78.01) * mm});
            skLineSegment(sketch, "E20.5.3.0", {"start": v(58.35, 53.12) * mm, "end": v(49.37, 62.1) * mm});
            skLineSegment(sketch, "E20.5.3.1", {"start": v(49.37, 44.14) * mm, "end": v(58.35, 53.12) * mm});
            skLineSegment(sketch, "E20.5.3.2", {"start": v(40.39, 53.12) * mm, "end": v(49.37, 44.14) * mm});
            skLineSegment(sketch, "E20.5.3.3", {"start": v(49.37, 62.1) * mm, "end": v(40.39, 53.12) * mm});
            skLineSegment(sketch, "E20.5.4.0", {"start": v(58.35, 28.23) * mm, "end": v(49.37, 37.21) * mm});
            skLineSegment(sketch, "E20.5.4.1", {"start": v(49.37, 19.25) * mm, "end": v(58.35, 28.23) * mm});
            skLineSegment(sketch, "E20.5.4.2", {"start": v(40.39, 28.23) * mm, "end": v(49.37, 19.25) * mm});
            skLineSegment(sketch, "E20.5.4.3", {"start": v(49.37, 37.21) * mm, "end": v(40.39, 28.23) * mm});
            skLineSegment(sketch, "E20.6.0.0", {"start": v(82.98, 127.8) * mm, "end": v(74, 136.78) * mm});
            skLineSegment(sketch, "E20.6.0.1", {"start": v(74, 118.82) * mm, "end": v(82.98, 127.8) * mm});
            skLineSegment(sketch, "E20.6.0.2", {"start": v(65.02, 127.8) * mm, "end": v(74, 118.82) * mm});
            skLineSegment(sketch, "E20.6.0.3", {"start": v(74, 136.78) * mm, "end": v(65.02, 127.8) * mm});
            skLineSegment(sketch, "E20.6.1.0", {"start": v(82.98, 102.9) * mm, "end": v(74, 111.89) * mm});
            skLineSegment(sketch, "E20.6.1.1", {"start": v(74, 93.93) * mm, "end": v(82.98, 102.9) * mm});
            skLineSegment(sketch, "E20.6.1.2", {"start": v(65.02, 102.9) * mm, "end": v(74, 93.93) * mm});
            skLineSegment(sketch, "E20.6.1.3", {"start": v(74, 111.89) * mm, "end": v(65.02, 102.9) * mm});
            skLineSegment(sketch, "E20.6.2.0", {"start": v(82.98, 78.01) * mm, "end": v(74, 87) * mm});
            skLineSegment(sketch, "E20.6.2.1", {"start": v(74, 69.03) * mm, "end": v(82.98, 78.01) * mm});
            skLineSegment(sketch, "E20.6.2.2", {"start": v(65.02, 78.01) * mm, "end": v(74, 69.03) * mm});
            skLineSegment(sketch, "E20.6.2.3", {"start": v(74, 87) * mm, "end": v(65.02, 78.01) * mm});
            skLineSegment(sketch, "E20.6.3.0", {"start": v(82.98, 53.12) * mm, "end": v(74, 62.1) * mm});
            skLineSegment(sketch, "E20.6.3.1", {"start": v(74, 44.14) * mm, "end": v(82.98, 53.12) * mm});
            skLineSegment(sketch, "E20.6.3.2", {"start": v(65.02, 53.12) * mm, "end": v(74, 44.14) * mm});
            skLineSegment(sketch, "E20.6.3.3", {"start": v(74, 62.1) * mm, "end": v(65.02, 53.12) * mm});
            skLineSegment(sketch, "E20.6.4.0", {"start": v(82.98, 28.23) * mm, "end": v(74, 37.21) * mm});
            skLineSegment(sketch, "E20.6.4.1", {"start": v(74, 19.25) * mm, "end": v(82.98, 28.23) * mm});
            skLineSegment(sketch, "E20.6.4.2", {"start": v(65.02, 28.23) * mm, "end": v(74, 19.25) * mm});
            skLineSegment(sketch, "E20.6.4.3", {"start": v(74, 37.21) * mm, "end": v(65.02, 28.23) * mm});
            skLineSegment(sketch, "E20.direction1", {"start": v(-64.84, 127.8) * mm, "end": v(-40.2, 127.8) * mm, "construction": true});
            skLineSegment(sketch, "E20.direction2", {"start": v(-64.84, 127.8) * mm, "end": v(-64.84, 102.9) * mm, "construction": true});
            skSolve(sketch);
        }
        {
            var Q0;
            Q0=qSketchRegion(id+"F8",true);
            extrude(context, id + "F9", {"entities" : qUnion([Q0]), "operationType" : NewBodyOperationType.REMOVE, "endBound" : BoundingType.THROUGH_ALL, "oppositeDirection" : true, "depth" : 25.4 * mm});
        }
        {
            var Q0;
            Q0=makeQuery(id+"F3.boolean.opBoolean","MERGE",FACE,{"derivedFrom":[makeQuery(id+"F1.opExtrude","SWEPT_FACE",FACE,{"disambiguationData":[OSD([sQuery(id+"F0.wireOp",EDGE,"E0.bottom")])]}),makeQuery(id+"F3.opExtrude","SWEPT_FACE",FACE,{"disambiguationData":[OSD([sQuery(id+"F2.wireOp",EDGE,"E1.bottom")])]})]});
            var sketch = newSketch(context, id + "F10", { "sketchPlane" : qUnion([Q0])});
            skLineSegment(sketch, "E21", {"start": v(-86.27, 149.23) * mm, "end": v(-95.25, 140.24) * mm});
            skLineSegment(sketch, "E22", {"start": v(-95.25, 140.24) * mm, "end": v(-86.27, 131.26) * mm});
            skLineSegment(sketch, "E23", {"start": v(-86.27, 131.26) * mm, "end": v(-77.29, 140.24) * mm});
            skLineSegment(sketch, "E24", {"start": v(-77.29, 140.24) * mm, "end": v(-86.27, 149.23) * mm});
            skLineSegment(sketch, "E25", {"start": v(-86.27, 131.26) * mm, "end": v(-56.15, 131.26) * mm, "construction": true});
            skLineSegment(sketch, "E26.0.1.0", {"start": v(-86.27, 106.37) * mm, "end": v(-77.29, 115.35) * mm});
            skLineSegment(sketch, "E26.0.1.1", {"start": v(-86.27, 124.33) * mm, "end": v(-95.25, 115.35) * mm});
            skLineSegment(sketch, "E26.0.1.2", {"start": v(-95.25, 115.35) * mm, "end": v(-86.27, 106.37) * mm});
            skLineSegment(sketch, "E26.0.1.3", {"start": v(-77.29, 115.35) * mm, "end": v(-86.27, 124.33) * mm});
            skLineSegment(sketch, "E26.0.2.0", {"start": v(-86.27, 81.48) * mm, "end": v(-77.29, 90.46) * mm});
            skLineSegment(sketch, "E26.0.2.1", {"start": v(-86.27, 99.44) * mm, "end": v(-95.25, 90.46) * mm});
            skLineSegment(sketch, "E26.0.2.2", {"start": v(-95.25, 90.46) * mm, "end": v(-86.27, 81.48) * mm});
            skLineSegment(sketch, "E26.0.2.3", {"start": v(-77.29, 90.46) * mm, "end": v(-86.27, 99.44) * mm});
            skLineSegment(sketch, "E26.0.3.0", {"start": v(-86.27, 56.59) * mm, "end": v(-77.29, 65.57) * mm});
            skLineSegment(sketch, "E26.0.3.1", {"start": v(-86.27, 74.55) * mm, "end": v(-95.25, 65.57) * mm});
            skLineSegment(sketch, "E26.0.3.2", {"start": v(-95.25, 65.57) * mm, "end": v(-86.27, 56.59) * mm});
            skLineSegment(sketch, "E26.0.3.3", {"start": v(-77.29, 65.57) * mm, "end": v(-86.27, 74.55) * mm});
            skLineSegment(sketch, "E26.0.4.0", {"start": v(-86.27, 31.7) * mm, "end": v(-77.29, 40.68) * mm});
            skLineSegment(sketch, "E26.0.4.1", {"start": v(-86.27, 49.66) * mm, "end": v(-95.25, 40.68) * mm});
            skLineSegment(sketch, "E26.0.4.2", {"start": v(-95.25, 40.68) * mm, "end": v(-86.27, 31.7) * mm});
            skLineSegment(sketch, "E26.0.4.3", {"start": v(-77.29, 40.68) * mm, "end": v(-86.27, 49.66) * mm});
            skLineSegment(sketch, "E26.0.5.0", {"start": v(-86.27, 6.8) * mm, "end": v(-77.29, 15.78) * mm});
            skLineSegment(sketch, "E26.0.5.1", {"start": v(-86.27, 24.77) * mm, "end": v(-95.25, 15.78) * mm});
            skLineSegment(sketch, "E26.0.5.2", {"start": v(-95.25, 15.78) * mm, "end": v(-86.27, 6.8) * mm});
            skLineSegment(sketch, "E26.0.5.3", {"start": v(-77.29, 15.78) * mm, "end": v(-86.27, 24.77) * mm});
            skLineSegment(sketch, "E26.1.0.0", {"start": v(-61.63, 131.26) * mm, "end": v(-52.65, 140.24) * mm});
            skLineSegment(sketch, "E26.1.0.1", {"start": v(-61.63, 149.23) * mm, "end": v(-70.61, 140.24) * mm});
            skLineSegment(sketch, "E26.1.0.2", {"start": v(-70.61, 140.24) * mm, "end": v(-61.63, 131.26) * mm});
            skLineSegment(sketch, "E26.1.0.3", {"start": v(-52.65, 140.24) * mm, "end": v(-61.63, 149.23) * mm});
            skLineSegment(sketch, "E26.1.1.0", {"start": v(-61.63, 106.37) * mm, "end": v(-52.65, 115.35) * mm});
            skLineSegment(sketch, "E26.1.1.1", {"start": v(-61.63, 124.33) * mm, "end": v(-70.61, 115.35) * mm});
            skLineSegment(sketch, "E26.1.1.2", {"start": v(-70.61, 115.35) * mm, "end": v(-61.63, 106.37) * mm});
            skLineSegment(sketch, "E26.1.1.3", {"start": v(-52.65, 115.35) * mm, "end": v(-61.63, 124.33) * mm});
            skLineSegment(sketch, "E26.1.2.0", {"start": v(-61.63, 81.48) * mm, "end": v(-52.65, 90.46) * mm});
            skLineSegment(sketch, "E26.1.2.1", {"start": v(-61.63, 99.44) * mm, "end": v(-70.61, 90.46) * mm});
            skLineSegment(sketch, "E26.1.2.2", {"start": v(-70.61, 90.46) * mm, "end": v(-61.63, 81.48) * mm});
            skLineSegment(sketch, "E26.1.2.3", {"start": v(-52.65, 90.46) * mm, "end": v(-61.63, 99.44) * mm});
            skLineSegment(sketch, "E26.1.3.0", {"start": v(-61.63, 56.59) * mm, "end": v(-52.65, 65.57) * mm});
            skLineSegment(sketch, "E26.1.3.1", {"start": v(-61.63, 74.55) * mm, "end": v(-70.61, 65.57) * mm});
            skLineSegment(sketch, "E26.1.3.2", {"start": v(-70.61, 65.57) * mm, "end": v(-61.63, 56.59) * mm});
            skLineSegment(sketch, "E26.1.3.3", {"start": v(-52.65, 65.57) * mm, "end": v(-61.63, 74.55) * mm});
            skLineSegment(sketch, "E26.1.4.0", {"start": v(-61.63, 31.7) * mm, "end": v(-52.65, 40.68) * mm});
            skLineSegment(sketch, "E26.1.4.1", {"start": v(-61.63, 49.66) * mm, "end": v(-70.61, 40.68) * mm});
            skLineSegment(sketch, "E26.1.4.2", {"start": v(-70.61, 40.68) * mm, "end": v(-61.63, 31.7) * mm});
            skLineSegment(sketch, "E26.1.4.3", {"start": v(-52.65, 40.68) * mm, "end": v(-61.63, 49.66) * mm});
            skLineSegment(sketch, "E26.1.5.0", {"start": v(-61.63, 6.8) * mm, "end": v(-52.65, 15.78) * mm});
            skLineSegment(sketch, "E26.1.5.1", {"start": v(-61.63, 24.77) * mm, "end": v(-70.61, 15.78) * mm});
            skLineSegment(sketch, "E26.1.5.2", {"start": v(-70.61, 15.78) * mm, "end": v(-61.63, 6.8) * mm});
            skLineSegment(sketch, "E26.1.5.3", {"start": v(-52.65, 15.78) * mm, "end": v(-61.63, 24.77) * mm});
            skLineSegment(sketch, "E26.2.0.0", {"start": v(-37, 131.26) * mm, "end": v(-28.01, 140.24) * mm});
            skLineSegment(sketch, "E26.2.0.1", {"start": v(-37, 149.23) * mm, "end": v(-45.97, 140.24) * mm});
            skLineSegment(sketch, "E26.2.0.2", {"start": v(-45.97, 140.24) * mm, "end": v(-37, 131.26) * mm});
            skLineSegment(sketch, "E26.2.0.3", {"start": v(-28.01, 140.24) * mm, "end": v(-37, 149.23) * mm});
            skLineSegment(sketch, "E26.2.1.0", {"start": v(-37, 106.37) * mm, "end": v(-28.01, 115.35) * mm});
            skLineSegment(sketch, "E26.2.1.1", {"start": v(-37, 124.33) * mm, "end": v(-45.97, 115.35) * mm});
            skLineSegment(sketch, "E26.2.1.2", {"start": v(-45.97, 115.35) * mm, "end": v(-37, 106.37) * mm});
            skLineSegment(sketch, "E26.2.1.3", {"start": v(-28.01, 115.35) * mm, "end": v(-37, 124.33) * mm});
            skLineSegment(sketch, "E26.2.2.0", {"start": v(-37, 81.48) * mm, "end": v(-28.01, 90.46) * mm});
            skLineSegment(sketch, "E26.2.2.1", {"start": v(-37, 99.44) * mm, "end": v(-45.97, 90.46) * mm});
            skLineSegment(sketch, "E26.2.2.2", {"start": v(-45.97, 90.46) * mm, "end": v(-37, 81.48) * mm});
            skLineSegment(sketch, "E26.2.2.3", {"start": v(-28.01, 90.46) * mm, "end": v(-37, 99.44) * mm});
            skLineSegment(sketch, "E26.2.3.0", {"start": v(-37, 56.59) * mm, "end": v(-28.01, 65.57) * mm});
            skLineSegment(sketch, "E26.2.3.1", {"start": v(-37, 74.55) * mm, "end": v(-45.97, 65.57) * mm});
            skLineSegment(sketch, "E26.2.3.2", {"start": v(-45.97, 65.57) * mm, "end": v(-37, 56.59) * mm});
            skLineSegment(sketch, "E26.2.3.3", {"start": v(-28.01, 65.57) * mm, "end": v(-37, 74.55) * mm});
            skLineSegment(sketch, "E26.2.4.0", {"start": v(-37, 31.7) * mm, "end": v(-28.01, 40.68) * mm});
            skLineSegment(sketch, "E26.2.4.1", {"start": v(-37, 49.66) * mm, "end": v(-45.97, 40.68) * mm});
            skLineSegment(sketch, "E26.2.4.2", {"start": v(-45.97, 40.68) * mm, "end": v(-37, 31.7) * mm});
            skLineSegment(sketch, "E26.2.4.3", {"start": v(-28.01, 40.68) * mm, "end": v(-37, 49.66) * mm});
            skLineSegment(sketch, "E26.2.5.0", {"start": v(-37, 6.8) * mm, "end": v(-28.01, 15.78) * mm});
            skLineSegment(sketch, "E26.2.5.1", {"start": v(-37, 24.77) * mm, "end": v(-45.97, 15.78) * mm});
            skLineSegment(sketch, "E26.2.5.2", {"start": v(-45.97, 15.78) * mm, "end": v(-37, 6.8) * mm});
            skLineSegment(sketch, "E26.2.5.3", {"start": v(-28.01, 15.78) * mm, "end": v(-37, 24.77) * mm});
            skLineSegment(sketch, "E26.3.0.0", {"start": v(-12.36, 131.26) * mm, "end": v(-3.38, 140.24) * mm});
            skLineSegment(sketch, "E26.3.0.1", {"start": v(-12.36, 149.23) * mm, "end": v(-21.34, 140.24) * mm});
            skLineSegment(sketch, "E26.3.0.2", {"start": v(-21.34, 140.24) * mm, "end": v(-12.36, 131.26) * mm});
            skLineSegment(sketch, "E26.3.0.3", {"start": v(-3.38, 140.24) * mm, "end": v(-12.36, 149.23) * mm});
            skLineSegment(sketch, "E26.3.1.0", {"start": v(-12.36, 106.37) * mm, "end": v(-3.38, 115.35) * mm});
            skLineSegment(sketch, "E26.3.1.1", {"start": v(-12.36, 124.33) * mm, "end": v(-21.34, 115.35) * mm});
            skLineSegment(sketch, "E26.3.1.2", {"start": v(-21.34, 115.35) * mm, "end": v(-12.36, 106.37) * mm});
            skLineSegment(sketch, "E26.3.1.3", {"start": v(-3.38, 115.35) * mm, "end": v(-12.36, 124.33) * mm});
            skLineSegment(sketch, "E26.3.2.0", {"start": v(-12.36, 81.48) * mm, "end": v(-3.38, 90.46) * mm});
            skLineSegment(sketch, "E26.3.2.1", {"start": v(-12.36, 99.44) * mm, "end": v(-21.34, 90.46) * mm});
            skLineSegment(sketch, "E26.3.2.2", {"start": v(-21.34, 90.46) * mm, "end": v(-12.36, 81.48) * mm});
            skLineSegment(sketch, "E26.3.2.3", {"start": v(-3.38, 90.46) * mm, "end": v(-12.36, 99.44) * mm});
            skLineSegment(sketch, "E26.3.3.0", {"start": v(-12.36, 56.59) * mm, "end": v(-3.38, 65.57) * mm});
            skLineSegment(sketch, "E26.3.3.1", {"start": v(-12.36, 74.55) * mm, "end": v(-21.34, 65.57) * mm});
            skLineSegment(sketch, "E26.3.3.2", {"start": v(-21.34, 65.57) * mm, "end": v(-12.36, 56.59) * mm});
            skLineSegment(sketch, "E26.3.3.3", {"start": v(-3.38, 65.57) * mm, "end": v(-12.36, 74.55) * mm});
            skLineSegment(sketch, "E26.3.4.0", {"start": v(-12.36, 31.7) * mm, "end": v(-3.38, 40.68) * mm});
            skLineSegment(sketch, "E26.3.4.1", {"start": v(-12.36, 49.66) * mm, "end": v(-21.34, 40.68) * mm});
            skLineSegment(sketch, "E26.3.4.2", {"start": v(-21.34, 40.68) * mm, "end": v(-12.36, 31.7) * mm});
            skLineSegment(sketch, "E26.3.4.3", {"start": v(-3.38, 40.68) * mm, "end": v(-12.36, 49.66) * mm});
            skLineSegment(sketch, "E26.3.5.0", {"start": v(-12.36, 6.8) * mm, "end": v(-3.38, 15.78) * mm});
            skLineSegment(sketch, "E26.3.5.1", {"start": v(-12.36, 24.77) * mm, "end": v(-21.34, 15.78) * mm});
            skLineSegment(sketch, "E26.3.5.2", {"start": v(-21.34, 15.78) * mm, "end": v(-12.36, 6.8) * mm});
            skLineSegment(sketch, "E26.3.5.3", {"start": v(-3.38, 15.78) * mm, "end": v(-12.36, 24.77) * mm});
            skLineSegment(sketch, "E26.4.0.0", {"start": v(12.28, 131.26) * mm, "end": v(21.26, 140.24) * mm});
            skLineSegment(sketch, "E26.4.0.1", {"start": v(12.28, 149.23) * mm, "end": v(3.3, 140.24) * mm});
            skLineSegment(sketch, "E26.4.0.2", {"start": v(3.3, 140.24) * mm, "end": v(12.28, 131.26) * mm});
            skLineSegment(sketch, "E26.4.0.3", {"start": v(21.26, 140.24) * mm, "end": v(12.28, 149.23) * mm});
            skLineSegment(sketch, "E26.4.1.0", {"start": v(12.28, 106.37) * mm, "end": v(21.26, 115.35) * mm});
            skLineSegment(sketch, "E26.4.1.1", {"start": v(12.28, 124.33) * mm, "end": v(3.3, 115.35) * mm});
            skLineSegment(sketch, "E26.4.1.2", {"start": v(3.3, 115.35) * mm, "end": v(12.28, 106.37) * mm});
            skLineSegment(sketch, "E26.4.1.3", {"start": v(21.26, 115.35) * mm, "end": v(12.28, 124.33) * mm});
            skLineSegment(sketch, "E26.4.2.0", {"start": v(12.28, 81.48) * mm, "end": v(21.26, 90.46) * mm});
            skLineSegment(sketch, "E26.4.2.1", {"start": v(12.28, 99.44) * mm, "end": v(3.3, 90.46) * mm});
            skLineSegment(sketch, "E26.4.2.2", {"start": v(3.3, 90.46) * mm, "end": v(12.28, 81.48) * mm});
            skLineSegment(sketch, "E26.4.2.3", {"start": v(21.26, 90.46) * mm, "end": v(12.28, 99.44) * mm});
            skLineSegment(sketch, "E26.4.3.0", {"start": v(12.28, 56.59) * mm, "end": v(21.26, 65.57) * mm});
            skLineSegment(sketch, "E26.4.3.1", {"start": v(12.28, 74.55) * mm, "end": v(3.3, 65.57) * mm});
            skLineSegment(sketch, "E26.4.3.2", {"start": v(3.3, 65.57) * mm, "end": v(12.28, 56.59) * mm});
            skLineSegment(sketch, "E26.4.3.3", {"start": v(21.26, 65.57) * mm, "end": v(12.28, 74.55) * mm});
            skLineSegment(sketch, "E26.4.4.0", {"start": v(12.28, 31.7) * mm, "end": v(21.26, 40.68) * mm});
            skLineSegment(sketch, "E26.4.4.1", {"start": v(12.28, 49.66) * mm, "end": v(3.3, 40.68) * mm});
            skLineSegment(sketch, "E26.4.4.2", {"start": v(3.3, 40.68) * mm, "end": v(12.28, 31.7) * mm});
            skLineSegment(sketch, "E26.4.4.3", {"start": v(21.26, 40.68) * mm, "end": v(12.28, 49.66) * mm});
            skLineSegment(sketch, "E26.4.5.0", {"start": v(12.28, 6.8) * mm, "end": v(21.26, 15.78) * mm});
            skLineSegment(sketch, "E26.4.5.1", {"start": v(12.28, 24.77) * mm, "end": v(3.3, 15.78) * mm});
            skLineSegment(sketch, "E26.4.5.2", {"start": v(3.3, 15.78) * mm, "end": v(12.28, 6.8) * mm});
            skLineSegment(sketch, "E26.4.5.3", {"start": v(21.26, 15.78) * mm, "end": v(12.28, 24.77) * mm});
            skLineSegment(sketch, "E26.5.0.0", {"start": v(36.92, 131.26) * mm, "end": v(45.9, 140.24) * mm});
            skLineSegment(sketch, "E26.5.0.1", {"start": v(36.92, 149.23) * mm, "end": v(27.94, 140.24) * mm});
            skLineSegment(sketch, "E26.5.0.2", {"start": v(27.94, 140.24) * mm, "end": v(36.92, 131.26) * mm});
            skLineSegment(sketch, "E26.5.0.3", {"start": v(45.9, 140.24) * mm, "end": v(36.92, 149.23) * mm});
            skLineSegment(sketch, "E26.5.1.0", {"start": v(36.92, 106.37) * mm, "end": v(45.9, 115.35) * mm});
            skLineSegment(sketch, "E26.5.1.1", {"start": v(36.92, 124.33) * mm, "end": v(27.94, 115.35) * mm});
            skLineSegment(sketch, "E26.5.1.2", {"start": v(27.94, 115.35) * mm, "end": v(36.92, 106.37) * mm});
            skLineSegment(sketch, "E26.5.1.3", {"start": v(45.9, 115.35) * mm, "end": v(36.92, 124.33) * mm});
            skLineSegment(sketch, "E26.5.2.0", {"start": v(36.92, 81.48) * mm, "end": v(45.9, 90.46) * mm});
            skLineSegment(sketch, "E26.5.2.1", {"start": v(36.92, 99.44) * mm, "end": v(27.94, 90.46) * mm});
            skLineSegment(sketch, "E26.5.2.2", {"start": v(27.94, 90.46) * mm, "end": v(36.92, 81.48) * mm});
            skLineSegment(sketch, "E26.5.2.3", {"start": v(45.9, 90.46) * mm, "end": v(36.92, 99.44) * mm});
            skLineSegment(sketch, "E26.5.3.0", {"start": v(36.92, 56.59) * mm, "end": v(45.9, 65.57) * mm});
            skLineSegment(sketch, "E26.5.3.1", {"start": v(36.92, 74.55) * mm, "end": v(27.94, 65.57) * mm});
            skLineSegment(sketch, "E26.5.3.2", {"start": v(27.94, 65.57) * mm, "end": v(36.92, 56.59) * mm});
            skLineSegment(sketch, "E26.5.3.3", {"start": v(45.9, 65.57) * mm, "end": v(36.92, 74.55) * mm});
            skLineSegment(sketch, "E26.5.4.0", {"start": v(36.92, 31.7) * mm, "end": v(45.9, 40.68) * mm});
            skLineSegment(sketch, "E26.5.4.1", {"start": v(36.92, 49.66) * mm, "end": v(27.94, 40.68) * mm});
            skLineSegment(sketch, "E26.5.4.2", {"start": v(27.94, 40.68) * mm, "end": v(36.92, 31.7) * mm});
            skLineSegment(sketch, "E26.5.4.3", {"start": v(45.9, 40.68) * mm, "end": v(36.92, 49.66) * mm});
            skLineSegment(sketch, "E26.5.5.0", {"start": v(36.92, 6.8) * mm, "end": v(45.9, 15.78) * mm});
            skLineSegment(sketch, "E26.5.5.1", {"start": v(36.92, 24.77) * mm, "end": v(27.94, 15.78) * mm});
            skLineSegment(sketch, "E26.5.5.2", {"start": v(27.94, 15.78) * mm, "end": v(36.92, 6.8) * mm});
            skLineSegment(sketch, "E26.5.5.3", {"start": v(45.9, 15.78) * mm, "end": v(36.92, 24.77) * mm});
            skLineSegment(sketch, "E26.6.0.0", {"start": v(61.56, 131.26) * mm, "end": v(70.54, 140.24) * mm});
            skLineSegment(sketch, "E26.6.0.1", {"start": v(61.56, 149.23) * mm, "end": v(52.58, 140.24) * mm});
            skLineSegment(sketch, "E26.6.0.2", {"start": v(52.58, 140.24) * mm, "end": v(61.56, 131.26) * mm});
            skLineSegment(sketch, "E26.6.0.3", {"start": v(70.54, 140.24) * mm, "end": v(61.56, 149.23) * mm});
            skLineSegment(sketch, "E26.6.1.0", {"start": v(61.56, 106.37) * mm, "end": v(70.54, 115.35) * mm});
            skLineSegment(sketch, "E26.6.1.1", {"start": v(61.56, 124.33) * mm, "end": v(52.58, 115.35) * mm});
            skLineSegment(sketch, "E26.6.1.2", {"start": v(52.58, 115.35) * mm, "end": v(61.56, 106.37) * mm});
            skLineSegment(sketch, "E26.6.1.3", {"start": v(70.54, 115.35) * mm, "end": v(61.56, 124.33) * mm});
            skLineSegment(sketch, "E26.6.2.0", {"start": v(61.56, 81.48) * mm, "end": v(70.54, 90.46) * mm});
            skLineSegment(sketch, "E26.6.2.1", {"start": v(61.56, 99.44) * mm, "end": v(52.58, 90.46) * mm});
            skLineSegment(sketch, "E26.6.2.2", {"start": v(52.58, 90.46) * mm, "end": v(61.56, 81.48) * mm});
            skLineSegment(sketch, "E26.6.2.3", {"start": v(70.54, 90.46) * mm, "end": v(61.56, 99.44) * mm});
            skLineSegment(sketch, "E26.6.3.0", {"start": v(61.56, 56.59) * mm, "end": v(70.54, 65.57) * mm});
            skLineSegment(sketch, "E26.6.3.1", {"start": v(61.56, 74.55) * mm, "end": v(52.58, 65.57) * mm});
            skLineSegment(sketch, "E26.6.3.2", {"start": v(52.58, 65.57) * mm, "end": v(61.56, 56.59) * mm});
            skLineSegment(sketch, "E26.6.3.3", {"start": v(70.54, 65.57) * mm, "end": v(61.56, 74.55) * mm});
            skLineSegment(sketch, "E26.6.4.0", {"start": v(61.56, 31.7) * mm, "end": v(70.54, 40.68) * mm});
            skLineSegment(sketch, "E26.6.4.1", {"start": v(61.56, 49.66) * mm, "end": v(52.58, 40.68) * mm});
            skLineSegment(sketch, "E26.6.4.2", {"start": v(52.58, 40.68) * mm, "end": v(61.56, 31.7) * mm});
            skLineSegment(sketch, "E26.6.4.3", {"start": v(70.54, 40.68) * mm, "end": v(61.56, 49.66) * mm});
            skLineSegment(sketch, "E26.6.5.0", {"start": v(61.56, 6.8) * mm, "end": v(70.54, 15.78) * mm});
            skLineSegment(sketch, "E26.6.5.1", {"start": v(61.56, 24.77) * mm, "end": v(52.58, 15.78) * mm});
            skLineSegment(sketch, "E26.6.5.2", {"start": v(52.58, 15.78) * mm, "end": v(61.56, 6.8) * mm});
            skLineSegment(sketch, "E26.6.5.3", {"start": v(70.54, 15.78) * mm, "end": v(61.56, 24.77) * mm});
            skLineSegment(sketch, "E26.7.0.0", {"start": v(86.2, 131.26) * mm, "end": v(95.18, 140.24) * mm});
            skLineSegment(sketch, "E26.7.0.1", {"start": v(86.2, 149.23) * mm, "end": v(77.22, 140.24) * mm});
            skLineSegment(sketch, "E26.7.0.2", {"start": v(77.22, 140.24) * mm, "end": v(86.2, 131.26) * mm});
            skLineSegment(sketch, "E26.7.0.3", {"start": v(95.18, 140.24) * mm, "end": v(86.2, 149.23) * mm});
            skLineSegment(sketch, "E26.7.1.0", {"start": v(86.2, 106.37) * mm, "end": v(95.18, 115.35) * mm});
            skLineSegment(sketch, "E26.7.1.1", {"start": v(86.2, 124.33) * mm, "end": v(77.22, 115.35) * mm});
            skLineSegment(sketch, "E26.7.1.2", {"start": v(77.22, 115.35) * mm, "end": v(86.2, 106.37) * mm});
            skLineSegment(sketch, "E26.7.1.3", {"start": v(95.18, 115.35) * mm, "end": v(86.2, 124.33) * mm});
            skLineSegment(sketch, "E26.7.2.0", {"start": v(86.2, 81.48) * mm, "end": v(95.18, 90.46) * mm});
            skLineSegment(sketch, "E26.7.2.1", {"start": v(86.2, 99.44) * mm, "end": v(77.22, 90.46) * mm});
            skLineSegment(sketch, "E26.7.2.2", {"start": v(77.22, 90.46) * mm, "end": v(86.2, 81.48) * mm});
            skLineSegment(sketch, "E26.7.2.3", {"start": v(95.18, 90.46) * mm, "end": v(86.2, 99.44) * mm});
            skLineSegment(sketch, "E26.7.3.0", {"start": v(86.2, 56.59) * mm, "end": v(95.18, 65.57) * mm});
            skLineSegment(sketch, "E26.7.3.1", {"start": v(86.2, 74.55) * mm, "end": v(77.22, 65.57) * mm});
            skLineSegment(sketch, "E26.7.3.2", {"start": v(77.22, 65.57) * mm, "end": v(86.2, 56.59) * mm});
            skLineSegment(sketch, "E26.7.3.3", {"start": v(95.18, 65.57) * mm, "end": v(86.2, 74.55) * mm});
            skLineSegment(sketch, "E26.7.4.0", {"start": v(86.2, 31.7) * mm, "end": v(95.18, 40.68) * mm});
            skLineSegment(sketch, "E26.7.4.1", {"start": v(86.2, 49.66) * mm, "end": v(77.22, 40.68) * mm});
            skLineSegment(sketch, "E26.7.4.2", {"start": v(77.22, 40.68) * mm, "end": v(86.2, 31.7) * mm});
            skLineSegment(sketch, "E26.7.4.3", {"start": v(95.18, 40.68) * mm, "end": v(86.2, 49.66) * mm});
            skLineSegment(sketch, "E26.7.5.0", {"start": v(86.2, 6.8) * mm, "end": v(95.18, 15.78) * mm});
            skLineSegment(sketch, "E26.7.5.1", {"start": v(86.2, 24.77) * mm, "end": v(77.22, 15.78) * mm});
            skLineSegment(sketch, "E26.7.5.2", {"start": v(77.22, 15.78) * mm, "end": v(86.2, 6.8) * mm});
            skLineSegment(sketch, "E26.7.5.3", {"start": v(95.18, 15.78) * mm, "end": v(86.2, 24.77) * mm});
            skLineSegment(sketch, "E26.direction1", {"start": v(-86.27, 131.26) * mm, "end": v(-61.63, 131.26) * mm, "construction": true});
            skLineSegment(sketch, "E26.direction2", {"start": v(-86.27, 131.26) * mm, "end": v(-86.27, 106.37) * mm, "construction": true});
            skSolve(sketch);
        }
        {
            var Q0;
            Q0=qSketchRegion(id+"F10",true);
            extrude(context, id + "F11", {"entities" : qUnion([Q0]), "operationType" : NewBodyOperationType.REMOVE, "endBound" : BoundingType.THROUGH_ALL, "oppositeDirection" : true, "depth" : 25.4 * mm});
        }
        {
            var Q0;
            Q0=makeQuery(id+"F3.boolean.opBoolean","MERGE",FACE,{"derivedFrom":[makeQuery(id+"F1.opExtrude","SWEPT_FACE",FACE,{"disambiguationData":[OSD([sQuery(id+"F0.wireOp",EDGE,"E0.bottom")])]}),makeQuery(id+"F3.opExtrude","SWEPT_FACE",FACE,{"disambiguationData":[OSD([sQuery(id+"F2.wireOp",EDGE,"E1.bottom")])]})]});
            var sketch = newSketch(context, id + "F12", { "sketchPlane" : qUnion([Q0])});
            skLineSegment(sketch, "E27", {"start": v(-73.82, 136.78) * mm, "end": v(-64.84, 127.8) * mm});
            skLineSegment(sketch, "E28", {"start": v(-64.84, 127.8) * mm, "end": v(-73.82, 118.82) * mm});
            skLineSegment(sketch, "E29", {"start": v(-73.82, 118.82) * mm, "end": v(-82.8, 127.8) * mm});
            skLineSegment(sketch, "E30", {"start": v(-82.8, 127.8) * mm, "end": v(-73.82, 136.78) * mm});
            skLineSegment(sketch, "E31.0.1.0", {"start": v(-82.8, 102.9) * mm, "end": v(-73.82, 111.89) * mm});
            skLineSegment(sketch, "E31.0.1.1", {"start": v(-73.82, 93.93) * mm, "end": v(-82.8, 102.9) * mm});
            skLineSegment(sketch, "E31.0.1.2", {"start": v(-64.84, 102.9) * mm, "end": v(-73.82, 93.93) * mm});
            skLineSegment(sketch, "E31.0.1.3", {"start": v(-73.82, 111.89) * mm, "end": v(-64.84, 102.9) * mm});
            skLineSegment(sketch, "E31.0.2.0", {"start": v(-82.8, 78.01) * mm, "end": v(-73.82, 87) * mm});
            skLineSegment(sketch, "E31.0.2.1", {"start": v(-73.82, 69.03) * mm, "end": v(-82.8, 78.01) * mm});
            skLineSegment(sketch, "E31.0.2.2", {"start": v(-64.84, 78.01) * mm, "end": v(-73.82, 69.03) * mm});
            skLineSegment(sketch, "E31.0.2.3", {"start": v(-73.82, 87) * mm, "end": v(-64.84, 78.01) * mm});
            skLineSegment(sketch, "E31.0.3.0", {"start": v(-82.8, 53.12) * mm, "end": v(-73.82, 62.1) * mm});
            skLineSegment(sketch, "E31.0.3.1", {"start": v(-73.82, 44.14) * mm, "end": v(-82.8, 53.12) * mm});
            skLineSegment(sketch, "E31.0.3.2", {"start": v(-64.84, 53.12) * mm, "end": v(-73.82, 44.14) * mm});
            skLineSegment(sketch, "E31.0.3.3", {"start": v(-73.82, 62.1) * mm, "end": v(-64.84, 53.12) * mm});
            skLineSegment(sketch, "E31.0.4.0", {"start": v(-82.8, 28.23) * mm, "end": v(-73.82, 37.21) * mm});
            skLineSegment(sketch, "E31.0.4.1", {"start": v(-73.82, 19.25) * mm, "end": v(-82.8, 28.23) * mm});
            skLineSegment(sketch, "E31.0.4.2", {"start": v(-64.84, 28.23) * mm, "end": v(-73.82, 19.25) * mm});
            skLineSegment(sketch, "E31.0.4.3", {"start": v(-73.82, 37.21) * mm, "end": v(-64.84, 28.23) * mm});
            skLineSegment(sketch, "E31.1.0.0", {"start": v(-58.17, 127.8) * mm, "end": v(-49.19, 136.78) * mm});
            skLineSegment(sketch, "E31.1.0.1", {"start": v(-49.19, 118.82) * mm, "end": v(-58.17, 127.8) * mm});
            skLineSegment(sketch, "E31.1.0.2", {"start": v(-40.2, 127.8) * mm, "end": v(-49.19, 118.82) * mm});
            skLineSegment(sketch, "E31.1.0.3", {"start": v(-49.19, 136.78) * mm, "end": v(-40.2, 127.8) * mm});
            skLineSegment(sketch, "E31.1.1.0", {"start": v(-58.17, 102.9) * mm, "end": v(-49.19, 111.89) * mm});
            skLineSegment(sketch, "E31.1.1.1", {"start": v(-49.19, 93.93) * mm, "end": v(-58.17, 102.9) * mm});
            skLineSegment(sketch, "E31.1.1.2", {"start": v(-40.2, 102.9) * mm, "end": v(-49.19, 93.93) * mm});
            skLineSegment(sketch, "E31.1.1.3", {"start": v(-49.19, 111.89) * mm, "end": v(-40.2, 102.9) * mm});
            skLineSegment(sketch, "E31.1.2.0", {"start": v(-58.17, 78.01) * mm, "end": v(-49.19, 87) * mm});
            skLineSegment(sketch, "E31.1.2.1", {"start": v(-49.19, 69.03) * mm, "end": v(-58.17, 78.01) * mm});
            skLineSegment(sketch, "E31.1.2.2", {"start": v(-40.2, 78.01) * mm, "end": v(-49.19, 69.03) * mm});
            skLineSegment(sketch, "E31.1.2.3", {"start": v(-49.19, 87) * mm, "end": v(-40.2, 78.01) * mm});
            skLineSegment(sketch, "E31.1.3.0", {"start": v(-58.17, 53.12) * mm, "end": v(-49.19, 62.1) * mm});
            skLineSegment(sketch, "E31.1.3.1", {"start": v(-49.19, 44.14) * mm, "end": v(-58.17, 53.12) * mm});
            skLineSegment(sketch, "E31.1.3.2", {"start": v(-40.2, 53.12) * mm, "end": v(-49.19, 44.14) * mm});
            skLineSegment(sketch, "E31.1.3.3", {"start": v(-49.19, 62.1) * mm, "end": v(-40.2, 53.12) * mm});
            skLineSegment(sketch, "E31.1.4.0", {"start": v(-58.17, 28.23) * mm, "end": v(-49.19, 37.21) * mm});
            skLineSegment(sketch, "E31.1.4.1", {"start": v(-49.19, 19.25) * mm, "end": v(-58.17, 28.23) * mm});
            skLineSegment(sketch, "E31.1.4.2", {"start": v(-40.2, 28.23) * mm, "end": v(-49.19, 19.25) * mm});
            skLineSegment(sketch, "E31.1.4.3", {"start": v(-49.19, 37.21) * mm, "end": v(-40.2, 28.23) * mm});
            skLineSegment(sketch, "E31.2.0.0", {"start": v(-33.53, 127.8) * mm, "end": v(-24.55, 136.78) * mm});
            skLineSegment(sketch, "E31.2.0.1", {"start": v(-24.55, 118.82) * mm, "end": v(-33.53, 127.8) * mm});
            skLineSegment(sketch, "E31.2.0.2", {"start": v(-15.57, 127.8) * mm, "end": v(-24.55, 118.82) * mm});
            skLineSegment(sketch, "E31.2.0.3", {"start": v(-24.55, 136.78) * mm, "end": v(-15.57, 127.8) * mm});
            skLineSegment(sketch, "E31.2.1.0", {"start": v(-33.53, 102.9) * mm, "end": v(-24.55, 111.89) * mm});
            skLineSegment(sketch, "E31.2.1.1", {"start": v(-24.55, 93.93) * mm, "end": v(-33.53, 102.9) * mm});
            skLineSegment(sketch, "E31.2.1.2", {"start": v(-15.57, 102.9) * mm, "end": v(-24.55, 93.93) * mm});
            skLineSegment(sketch, "E31.2.1.3", {"start": v(-24.55, 111.89) * mm, "end": v(-15.57, 102.9) * mm});
            skLineSegment(sketch, "E31.2.2.0", {"start": v(-33.53, 78.01) * mm, "end": v(-24.55, 87) * mm});
            skLineSegment(sketch, "E31.2.2.1", {"start": v(-24.55, 69.03) * mm, "end": v(-33.53, 78.01) * mm});
            skLineSegment(sketch, "E31.2.2.2", {"start": v(-15.57, 78.01) * mm, "end": v(-24.55, 69.03) * mm});
            skLineSegment(sketch, "E31.2.2.3", {"start": v(-24.55, 87) * mm, "end": v(-15.57, 78.01) * mm});
            skLineSegment(sketch, "E31.2.3.0", {"start": v(-33.53, 53.12) * mm, "end": v(-24.55, 62.1) * mm});
            skLineSegment(sketch, "E31.2.3.1", {"start": v(-24.55, 44.14) * mm, "end": v(-33.53, 53.12) * mm});
            skLineSegment(sketch, "E31.2.3.2", {"start": v(-15.57, 53.12) * mm, "end": v(-24.55, 44.14) * mm});
            skLineSegment(sketch, "E31.2.3.3", {"start": v(-24.55, 62.1) * mm, "end": v(-15.57, 53.12) * mm});
            skLineSegment(sketch, "E31.2.4.0", {"start": v(-33.53, 28.23) * mm, "end": v(-24.55, 37.21) * mm});
            skLineSegment(sketch, "E31.2.4.1", {"start": v(-24.55, 19.25) * mm, "end": v(-33.53, 28.23) * mm});
            skLineSegment(sketch, "E31.2.4.2", {"start": v(-15.57, 28.23) * mm, "end": v(-24.55, 19.25) * mm});
            skLineSegment(sketch, "E31.2.4.3", {"start": v(-24.55, 37.21) * mm, "end": v(-15.57, 28.23) * mm});
            skLineSegment(sketch, "E31.3.0.0", {"start": v(-8.9, 127.8) * mm, "end": v(0.1, 136.78) * mm});
            skLineSegment(sketch, "E31.3.0.1", {"start": v(0.1, 118.82) * mm, "end": v(-8.9, 127.8) * mm});
            skLineSegment(sketch, "E31.3.0.2", {"start": v(9.07, 127.8) * mm, "end": v(0.1, 118.82) * mm});
            skLineSegment(sketch, "E31.3.0.3", {"start": v(0.1, 136.78) * mm, "end": v(9.07, 127.8) * mm});
            skLineSegment(sketch, "E31.3.1.0", {"start": v(-8.9, 102.9) * mm, "end": v(0.1, 111.89) * mm});
            skLineSegment(sketch, "E31.3.1.1", {"start": v(0.1, 93.93) * mm, "end": v(-8.9, 102.9) * mm});
            skLineSegment(sketch, "E31.3.1.2", {"start": v(9.07, 102.9) * mm, "end": v(0.1, 93.93) * mm});
            skLineSegment(sketch, "E31.3.1.3", {"start": v(0.1, 111.89) * mm, "end": v(9.07, 102.9) * mm});
            skLineSegment(sketch, "E31.3.2.0", {"start": v(-8.9, 78.01) * mm, "end": v(0.1, 87) * mm});
            skLineSegment(sketch, "E31.3.2.1", {"start": v(0.1, 69.03) * mm, "end": v(-8.9, 78.01) * mm});
            skLineSegment(sketch, "E31.3.2.2", {"start": v(9.07, 78.01) * mm, "end": v(0.1, 69.03) * mm});
            skLineSegment(sketch, "E31.3.2.3", {"start": v(0.1, 87) * mm, "end": v(9.07, 78.01) * mm});
            skLineSegment(sketch, "E31.3.3.0", {"start": v(-8.9, 53.12) * mm, "end": v(0.1, 62.1) * mm});
            skLineSegment(sketch, "E31.3.3.1", {"start": v(0.1, 44.14) * mm, "end": v(-8.9, 53.12) * mm});
            skLineSegment(sketch, "E31.3.3.2", {"start": v(9.07, 53.12) * mm, "end": v(0.1, 44.14) * mm});
            skLineSegment(sketch, "E31.3.3.3", {"start": v(0.1, 62.1) * mm, "end": v(9.07, 53.12) * mm});
            skLineSegment(sketch, "E31.3.4.0", {"start": v(-8.9, 28.23) * mm, "end": v(0.1, 37.21) * mm});
            skLineSegment(sketch, "E31.3.4.1", {"start": v(0.1, 19.25) * mm, "end": v(-8.9, 28.23) * mm});
            skLineSegment(sketch, "E31.3.4.2", {"start": v(9.07, 28.23) * mm, "end": v(0.1, 19.25) * mm});
            skLineSegment(sketch, "E31.3.4.3", {"start": v(0.1, 37.21) * mm, "end": v(9.07, 28.23) * mm});
            skLineSegment(sketch, "E31.4.0.0", {"start": v(15.75, 127.8) * mm, "end": v(24.73, 136.78) * mm});
            skLineSegment(sketch, "E31.4.0.1", {"start": v(24.73, 118.82) * mm, "end": v(15.75, 127.8) * mm});
            skLineSegment(sketch, "E31.4.0.2", {"start": v(33.7, 127.8) * mm, "end": v(24.73, 118.82) * mm});
            skLineSegment(sketch, "E31.4.0.3", {"start": v(24.73, 136.78) * mm, "end": v(33.7, 127.8) * mm});
            skLineSegment(sketch, "E31.4.1.0", {"start": v(15.75, 102.9) * mm, "end": v(24.73, 111.89) * mm});
            skLineSegment(sketch, "E31.4.1.1", {"start": v(24.73, 93.93) * mm, "end": v(15.75, 102.9) * mm});
            skLineSegment(sketch, "E31.4.1.2", {"start": v(33.7, 102.9) * mm, "end": v(24.73, 93.93) * mm});
            skLineSegment(sketch, "E31.4.1.3", {"start": v(24.73, 111.89) * mm, "end": v(33.7, 102.9) * mm});
            skLineSegment(sketch, "E31.4.2.0", {"start": v(15.75, 78.01) * mm, "end": v(24.73, 87) * mm});
            skLineSegment(sketch, "E31.4.2.1", {"start": v(24.73, 69.03) * mm, "end": v(15.75, 78.01) * mm});
            skLineSegment(sketch, "E31.4.2.2", {"start": v(33.7, 78.01) * mm, "end": v(24.73, 69.03) * mm});
            skLineSegment(sketch, "E31.4.2.3", {"start": v(24.73, 87) * mm, "end": v(33.7, 78.01) * mm});
            skLineSegment(sketch, "E31.4.3.0", {"start": v(15.75, 53.12) * mm, "end": v(24.73, 62.1) * mm});
            skLineSegment(sketch, "E31.4.3.1", {"start": v(24.73, 44.14) * mm, "end": v(15.75, 53.12) * mm});
            skLineSegment(sketch, "E31.4.3.2", {"start": v(33.7, 53.12) * mm, "end": v(24.73, 44.14) * mm});
            skLineSegment(sketch, "E31.4.3.3", {"start": v(24.73, 62.1) * mm, "end": v(33.7, 53.12) * mm});
            skLineSegment(sketch, "E31.4.4.0", {"start": v(15.75, 28.23) * mm, "end": v(24.73, 37.21) * mm});
            skLineSegment(sketch, "E31.4.4.1", {"start": v(24.73, 19.25) * mm, "end": v(15.75, 28.23) * mm});
            skLineSegment(sketch, "E31.4.4.2", {"start": v(33.7, 28.23) * mm, "end": v(24.73, 19.25) * mm});
            skLineSegment(sketch, "E31.4.4.3", {"start": v(24.73, 37.21) * mm, "end": v(33.7, 28.23) * mm});
            skLineSegment(sketch, "E31.5.0.0", {"start": v(40.39, 127.8) * mm, "end": v(49.37, 136.78) * mm});
            skLineSegment(sketch, "E31.5.0.1", {"start": v(49.37, 118.82) * mm, "end": v(40.39, 127.8) * mm});
            skLineSegment(sketch, "E31.5.0.2", {"start": v(58.35, 127.8) * mm, "end": v(49.37, 118.82) * mm});
            skLineSegment(sketch, "E31.5.0.3", {"start": v(49.37, 136.78) * mm, "end": v(58.35, 127.8) * mm});
            skLineSegment(sketch, "E31.5.1.0", {"start": v(40.39, 102.9) * mm, "end": v(49.37, 111.89) * mm});
            skLineSegment(sketch, "E31.5.1.1", {"start": v(49.37, 93.93) * mm, "end": v(40.39, 102.9) * mm});
            skLineSegment(sketch, "E31.5.1.2", {"start": v(58.35, 102.9) * mm, "end": v(49.37, 93.93) * mm});
            skLineSegment(sketch, "E31.5.1.3", {"start": v(49.37, 111.89) * mm, "end": v(58.35, 102.9) * mm});
            skLineSegment(sketch, "E31.5.2.0", {"start": v(40.39, 78.01) * mm, "end": v(49.37, 87) * mm});
            skLineSegment(sketch, "E31.5.2.1", {"start": v(49.37, 69.03) * mm, "end": v(40.39, 78.01) * mm});
            skLineSegment(sketch, "E31.5.2.2", {"start": v(58.35, 78.01) * mm, "end": v(49.37, 69.03) * mm});
            skLineSegment(sketch, "E31.5.2.3", {"start": v(49.37, 87) * mm, "end": v(58.35, 78.01) * mm});
            skLineSegment(sketch, "E31.5.3.0", {"start": v(40.39, 53.12) * mm, "end": v(49.37, 62.1) * mm});
            skLineSegment(sketch, "E31.5.3.1", {"start": v(49.37, 44.14) * mm, "end": v(40.39, 53.12) * mm});
            skLineSegment(sketch, "E31.5.3.2", {"start": v(58.35, 53.12) * mm, "end": v(49.37, 44.14) * mm});
            skLineSegment(sketch, "E31.5.3.3", {"start": v(49.37, 62.1) * mm, "end": v(58.35, 53.12) * mm});
            skLineSegment(sketch, "E31.5.4.0", {"start": v(40.39, 28.23) * mm, "end": v(49.37, 37.21) * mm});
            skLineSegment(sketch, "E31.5.4.1", {"start": v(49.37, 19.25) * mm, "end": v(40.39, 28.23) * mm});
            skLineSegment(sketch, "E31.5.4.2", {"start": v(58.35, 28.23) * mm, "end": v(49.37, 19.25) * mm});
            skLineSegment(sketch, "E31.5.4.3", {"start": v(49.37, 37.21) * mm, "end": v(58.35, 28.23) * mm});
            skLineSegment(sketch, "E31.6.0.0", {"start": v(65.02, 127.8) * mm, "end": v(74, 136.78) * mm});
            skLineSegment(sketch, "E31.6.0.1", {"start": v(74, 118.82) * mm, "end": v(65.02, 127.8) * mm});
            skLineSegment(sketch, "E31.6.0.2", {"start": v(82.98, 127.8) * mm, "end": v(74, 118.82) * mm});
            skLineSegment(sketch, "E31.6.0.3", {"start": v(74, 136.78) * mm, "end": v(82.98, 127.8) * mm});
            skLineSegment(sketch, "E31.6.1.0", {"start": v(65.02, 102.9) * mm, "end": v(74, 111.89) * mm});
            skLineSegment(sketch, "E31.6.1.1", {"start": v(74, 93.93) * mm, "end": v(65.02, 102.9) * mm});
            skLineSegment(sketch, "E31.6.1.2", {"start": v(82.98, 102.9) * mm, "end": v(74, 93.93) * mm});
            skLineSegment(sketch, "E31.6.1.3", {"start": v(74, 111.89) * mm, "end": v(82.98, 102.9) * mm});
            skLineSegment(sketch, "E31.6.2.0", {"start": v(65.02, 78.01) * mm, "end": v(74, 87) * mm});
            skLineSegment(sketch, "E31.6.2.1", {"start": v(74, 69.03) * mm, "end": v(65.02, 78.01) * mm});
            skLineSegment(sketch, "E31.6.2.2", {"start": v(82.98, 78.01) * mm, "end": v(74, 69.03) * mm});
            skLineSegment(sketch, "E31.6.2.3", {"start": v(74, 87) * mm, "end": v(82.98, 78.01) * mm});
            skLineSegment(sketch, "E31.6.3.0", {"start": v(65.02, 53.12) * mm, "end": v(74, 62.1) * mm});
            skLineSegment(sketch, "E31.6.3.1", {"start": v(74, 44.14) * mm, "end": v(65.02, 53.12) * mm});
            skLineSegment(sketch, "E31.6.3.2", {"start": v(82.98, 53.12) * mm, "end": v(74, 44.14) * mm});
            skLineSegment(sketch, "E31.6.3.3", {"start": v(74, 62.1) * mm, "end": v(82.98, 53.12) * mm});
            skLineSegment(sketch, "E31.6.4.0", {"start": v(65.02, 28.23) * mm, "end": v(74, 37.21) * mm});
            skLineSegment(sketch, "E31.6.4.1", {"start": v(74, 19.25) * mm, "end": v(65.02, 28.23) * mm});
            skLineSegment(sketch, "E31.6.4.2", {"start": v(82.98, 28.23) * mm, "end": v(74, 19.25) * mm});
            skLineSegment(sketch, "E31.6.4.3", {"start": v(74, 37.21) * mm, "end": v(82.98, 28.23) * mm});
            skLineSegment(sketch, "E31.direction1", {"start": v(-82.8, 127.8) * mm, "end": v(-58.17, 127.8) * mm, "construction": true});
            skLineSegment(sketch, "E31.direction2", {"start": v(-82.8, 127.8) * mm, "end": v(-82.8, 102.9) * mm, "construction": true});
            skSolve(sketch);
        }
        {
            var Q0;
            Q0=qSketchRegion(id+"F12",true);
            extrude(context, id + "F13", {"entities" : qUnion([Q0]), "operationType" : NewBodyOperationType.REMOVE, "endBound" : BoundingType.THROUGH_ALL, "oppositeDirection" : true, "depth" : 25.4 * mm});
        }
        {
            var Q0;
            Q0=makeQuery(id+"F3.boolean.opBoolean","MERGE",FACE,{"derivedFrom":[makeQuery(id+"F1.opExtrude","SWEPT_FACE",FACE,{"disambiguationData":[OSD([sQuery(id+"F0.wireOp",EDGE,"E0.top")])]}),makeQuery(id+"F3.opExtrude","SWEPT_FACE",FACE,{"disambiguationData":[OSD([sQuery(id+"F2.wireOp",EDGE,"E1.top")])]})]});
            var sketch = newSketch(context, id + "F14", { "sketchPlane" : qUnion([Q0])});
            skLineSegment(sketch, "E32", {"start": v(-76.2, 155.58) * mm, "end": v(-63.5, 88.9) * mm});
            skLineSegment(sketch, "E33", {"start": v(-63.5, 88.9) * mm, "end": v(63.5, 88.9) * mm});
            skLineSegment(sketch, "E34", {"start": v(63.5, 88.9) * mm, "end": v(76.2, 155.58) * mm});
            skLineSegment(sketch, "E35.0", {"start": v(68.75, 82.55) * mm, "end": v(82.44, 154.39) * mm});
            skLineSegment(sketch, "E35.1", {"start": v(-68.75, 82.55) * mm, "end": v(68.75, 82.55) * mm});
            skLineSegment(sketch, "E35.2", {"start": v(-82.66, 155.58) * mm, "end": v(-68.75, 82.55) * mm});
            skLineSegment(sketch, "E36", {"start": v(-82.66, 155.58) * mm, "end": v(-76.2, 155.58) * mm});
            skLineSegment(sketch, "E37", {"start": v(82.44, 154.39) * mm, "end": v(82.44, 155.58) * mm});
            skLineSegment(sketch, "E38", {"start": v(82.44, 155.58) * mm, "end": v(76.2, 155.58) * mm});
            skSolve(sketch);
        }
        {
            var Q0;
            Q0=qSketchRegion(id+"F14",true);
            extrude(context, id + "F15", {"entities" : qUnion([Q0]), "operationType" : NewBodyOperationType.ADD, "oppositeDirection" : true, "depth" : 3.17 * mm});
        }
        {
            var Q0;
            Q0=makeQuery(id+"F1.opExtrude","CAP_FACE",FACE,{"disambiguationData":[OSD([sQuery(id+"F0.wireOp",EDGE,"E0.bottom"),sQuery(id+"F0.wireOp",EDGE,"E0.top"),sQuery(id+"F0.wireOp",EDGE,"E0.left"),sQuery(id+"F0.wireOp",EDGE,"E0.right")])],"isStart":false});
            var sketch = newSketch(context, id + "F16", { "sketchPlane" : qUnion([Q0])});
            skLineSegment(sketch, "E39.bottom", {"start": v(-73.03, 73.02) * mm, "end": v(-92.08, 73.02) * mm});
            skLineSegment(sketch, "E39.top", {"start": v(-73.03, 92.07) * mm, "end": v(-92.08, 92.07) * mm});
            skLineSegment(sketch, "E39.left", {"start": v(-73.03, 73.02) * mm, "end": v(-73.03, 92.07) * mm});
            skLineSegment(sketch, "E39.right", {"start": v(-92.08, 73.02) * mm, "end": v(-92.08, 92.07) * mm});
            skPoint(sketch, "E39.middle", {"position": v(-82.55, 82.55) * mm});
            skLineSegment(sketch, "E40.0.1.0", {"start": v(-73.03, 45.6) * mm, "end": v(-92.08, 45.6) * mm});
            skLineSegment(sketch, "E40.0.1.1", {"start": v(-92.08, 45.6) * mm, "end": v(-92.08, 64.64) * mm});
            skLineSegment(sketch, "E40.0.1.2", {"start": v(-73.03, 64.64) * mm, "end": v(-92.08, 64.64) * mm});
            skLineSegment(sketch, "E40.0.1.3", {"start": v(-73.03, 45.6) * mm, "end": v(-73.03, 64.64) * mm});
            skLineSegment(sketch, "E40.0.2.0", {"start": v(-73.03, 18.16) * mm, "end": v(-92.08, 18.16) * mm});
            skLineSegment(sketch, "E40.0.2.1", {"start": v(-92.08, 18.16) * mm, "end": v(-92.08, 37.21) * mm});
            skLineSegment(sketch, "E40.0.2.2", {"start": v(-73.03, 37.21) * mm, "end": v(-92.08, 37.21) * mm});
            skLineSegment(sketch, "E40.0.2.3", {"start": v(-73.03, 18.16) * mm, "end": v(-73.03, 37.21) * mm});
            skLineSegment(sketch, "E40.0.3.0", {"start": v(-73.03, -9.27) * mm, "end": v(-92.08, -9.27) * mm});
            skLineSegment(sketch, "E40.0.3.1", {"start": v(-92.08, -9.27) * mm, "end": v(-92.08, 9.78) * mm});
            skLineSegment(sketch, "E40.0.3.2", {"start": v(-73.03, 9.78) * mm, "end": v(-92.08, 9.78) * mm});
            skLineSegment(sketch, "E40.0.3.3", {"start": v(-73.03, -9.27) * mm, "end": v(-73.03, 9.78) * mm});
            skLineSegment(sketch, "E40.0.4.0", {"start": v(-73.03, -36.7) * mm, "end": v(-92.08, -36.7) * mm});
            skLineSegment(sketch, "E40.0.4.1", {"start": v(-92.08, -36.7) * mm, "end": v(-92.08, -17.65) * mm});
            skLineSegment(sketch, "E40.0.4.2", {"start": v(-73.03, -17.65) * mm, "end": v(-92.08, -17.65) * mm});
            skLineSegment(sketch, "E40.0.4.3", {"start": v(-73.03, -36.7) * mm, "end": v(-73.03, -17.65) * mm});
            skLineSegment(sketch, "E40.0.5.0", {"start": v(-73.03, -64.14) * mm, "end": v(-92.08, -64.14) * mm});
            skLineSegment(sketch, "E40.0.5.1", {"start": v(-92.08, -64.14) * mm, "end": v(-92.08, -45.09) * mm});
            skLineSegment(sketch, "E40.0.5.2", {"start": v(-73.03, -45.09) * mm, "end": v(-92.08, -45.09) * mm});
            skLineSegment(sketch, "E40.0.5.3", {"start": v(-73.03, -64.14) * mm, "end": v(-73.03, -45.09) * mm});
            skLineSegment(sketch, "E40.0.6.0", {"start": v(-73.03, -91.57) * mm, "end": v(-92.08, -91.57) * mm});
            skLineSegment(sketch, "E40.0.6.1", {"start": v(-92.08, -91.57) * mm, "end": v(-92.08, -72.52) * mm});
            skLineSegment(sketch, "E40.0.6.2", {"start": v(-73.03, -72.52) * mm, "end": v(-92.08, -72.52) * mm});
            skLineSegment(sketch, "E40.0.6.3", {"start": v(-73.03, -91.57) * mm, "end": v(-73.03, -72.52) * mm});
            skLineSegment(sketch, "E40.1.0.0", {"start": v(-45.6, 73.02) * mm, "end": v(-64.64, 73.02) * mm});
            skLineSegment(sketch, "E40.1.0.1", {"start": v(-64.64, 73.02) * mm, "end": v(-64.64, 92.07) * mm});
            skLineSegment(sketch, "E40.1.0.2", {"start": v(-45.6, 92.07) * mm, "end": v(-64.64, 92.07) * mm});
            skLineSegment(sketch, "E40.1.0.3", {"start": v(-45.6, 73.02) * mm, "end": v(-45.6, 92.07) * mm});
            skLineSegment(sketch, "E40.1.1.0", {"start": v(-45.6, 45.6) * mm, "end": v(-64.64, 45.6) * mm});
            skLineSegment(sketch, "E40.1.1.1", {"start": v(-64.64, 45.6) * mm, "end": v(-64.64, 64.64) * mm});
            skLineSegment(sketch, "E40.1.1.2", {"start": v(-45.6, 64.64) * mm, "end": v(-64.64, 64.64) * mm});
            skLineSegment(sketch, "E40.1.1.3", {"start": v(-45.6, 45.6) * mm, "end": v(-45.6, 64.64) * mm});
            skLineSegment(sketch, "E40.1.2.0", {"start": v(-45.6, 18.16) * mm, "end": v(-64.64, 18.16) * mm});
            skLineSegment(sketch, "E40.1.2.1", {"start": v(-64.64, 18.16) * mm, "end": v(-64.64, 37.21) * mm});
            skLineSegment(sketch, "E40.1.2.2", {"start": v(-45.6, 37.21) * mm, "end": v(-64.64, 37.21) * mm});
            skLineSegment(sketch, "E40.1.2.3", {"start": v(-45.6, 18.16) * mm, "end": v(-45.6, 37.21) * mm});
            skLineSegment(sketch, "E40.1.3.0", {"start": v(-45.6, -9.27) * mm, "end": v(-64.64, -9.27) * mm});
            skLineSegment(sketch, "E40.1.3.1", {"start": v(-64.64, -9.27) * mm, "end": v(-64.64, 9.78) * mm});
            skLineSegment(sketch, "E40.1.3.2", {"start": v(-45.6, 9.78) * mm, "end": v(-64.64, 9.78) * mm});
            skLineSegment(sketch, "E40.1.3.3", {"start": v(-45.6, -9.27) * mm, "end": v(-45.6, 9.78) * mm});
            skLineSegment(sketch, "E40.1.4.0", {"start": v(-45.6, -36.7) * mm, "end": v(-64.64, -36.7) * mm});
            skLineSegment(sketch, "E40.1.4.1", {"start": v(-64.64, -36.7) * mm, "end": v(-64.64, -17.65) * mm});
            skLineSegment(sketch, "E40.1.4.2", {"start": v(-45.6, -17.65) * mm, "end": v(-64.64, -17.65) * mm});
            skLineSegment(sketch, "E40.1.4.3", {"start": v(-45.6, -36.7) * mm, "end": v(-45.6, -17.65) * mm});
            skLineSegment(sketch, "E40.1.5.0", {"start": v(-45.6, -64.14) * mm, "end": v(-64.64, -64.14) * mm});
            skLineSegment(sketch, "E40.1.5.1", {"start": v(-64.64, -64.14) * mm, "end": v(-64.64, -45.09) * mm});
            skLineSegment(sketch, "E40.1.5.2", {"start": v(-45.6, -45.09) * mm, "end": v(-64.64, -45.09) * mm});
            skLineSegment(sketch, "E40.1.5.3", {"start": v(-45.6, -64.14) * mm, "end": v(-45.6, -45.09) * mm});
            skLineSegment(sketch, "E40.1.6.0", {"start": v(-45.6, -91.57) * mm, "end": v(-64.64, -91.57) * mm});
            skLineSegment(sketch, "E40.1.6.1", {"start": v(-64.64, -91.57) * mm, "end": v(-64.64, -72.52) * mm});
            skLineSegment(sketch, "E40.1.6.2", {"start": v(-45.6, -72.52) * mm, "end": v(-64.64, -72.52) * mm});
            skLineSegment(sketch, "E40.1.6.3", {"start": v(-45.6, -91.57) * mm, "end": v(-45.6, -72.52) * mm});
            skLineSegment(sketch, "E40.2.0.0", {"start": v(-18.16, 73.02) * mm, "end": v(-37.21, 73.02) * mm});
            skLineSegment(sketch, "E40.2.0.1", {"start": v(-37.21, 73.02) * mm, "end": v(-37.21, 92.07) * mm});
            skLineSegment(sketch, "E40.2.0.2", {"start": v(-18.16, 92.07) * mm, "end": v(-37.21, 92.07) * mm});
            skLineSegment(sketch, "E40.2.0.3", {"start": v(-18.16, 73.02) * mm, "end": v(-18.16, 92.07) * mm});
            skLineSegment(sketch, "E40.2.1.0", {"start": v(-18.16, 45.6) * mm, "end": v(-37.21, 45.6) * mm});
            skLineSegment(sketch, "E40.2.1.1", {"start": v(-37.21, 45.6) * mm, "end": v(-37.21, 64.64) * mm});
            skLineSegment(sketch, "E40.2.1.2", {"start": v(-18.16, 64.64) * mm, "end": v(-37.21, 64.64) * mm});
            skLineSegment(sketch, "E40.2.1.3", {"start": v(-18.16, 45.6) * mm, "end": v(-18.16, 64.64) * mm});
            skLineSegment(sketch, "E40.2.2.0", {"start": v(-18.16, 18.16) * mm, "end": v(-37.21, 18.16) * mm});
            skLineSegment(sketch, "E40.2.2.1", {"start": v(-37.21, 18.16) * mm, "end": v(-37.21, 37.21) * mm});
            skLineSegment(sketch, "E40.2.2.2", {"start": v(-18.16, 37.21) * mm, "end": v(-37.21, 37.21) * mm});
            skLineSegment(sketch, "E40.2.2.3", {"start": v(-18.16, 18.16) * mm, "end": v(-18.16, 37.21) * mm});
            skLineSegment(sketch, "E40.2.3.0", {"start": v(-18.16, -9.27) * mm, "end": v(-37.21, -9.27) * mm});
            skLineSegment(sketch, "E40.2.3.1", {"start": v(-37.21, -9.27) * mm, "end": v(-37.21, 9.78) * mm});
            skLineSegment(sketch, "E40.2.3.2", {"start": v(-18.16, 9.78) * mm, "end": v(-37.21, 9.78) * mm});
            skLineSegment(sketch, "E40.2.3.3", {"start": v(-18.16, -9.27) * mm, "end": v(-18.16, 9.78) * mm});
            skLineSegment(sketch, "E40.2.4.0", {"start": v(-18.16, -36.7) * mm, "end": v(-37.21, -36.7) * mm});
            skLineSegment(sketch, "E40.2.4.1", {"start": v(-37.21, -36.7) * mm, "end": v(-37.21, -17.65) * mm});
            skLineSegment(sketch, "E40.2.4.2", {"start": v(-18.16, -17.65) * mm, "end": v(-37.21, -17.65) * mm});
            skLineSegment(sketch, "E40.2.4.3", {"start": v(-18.16, -36.7) * mm, "end": v(-18.16, -17.65) * mm});
            skLineSegment(sketch, "E40.2.5.0", {"start": v(-18.16, -64.14) * mm, "end": v(-37.21, -64.14) * mm});
            skLineSegment(sketch, "E40.2.5.1", {"start": v(-37.21, -64.14) * mm, "end": v(-37.21, -45.09) * mm});
            skLineSegment(sketch, "E40.2.5.2", {"start": v(-18.16, -45.09) * mm, "end": v(-37.21, -45.09) * mm});
            skLineSegment(sketch, "E40.2.5.3", {"start": v(-18.16, -64.14) * mm, "end": v(-18.16, -45.09) * mm});
            skLineSegment(sketch, "E40.2.6.0", {"start": v(-18.16, -91.57) * mm, "end": v(-37.21, -91.57) * mm});
            skLineSegment(sketch, "E40.2.6.1", {"start": v(-37.21, -91.57) * mm, "end": v(-37.21, -72.52) * mm});
            skLineSegment(sketch, "E40.2.6.2", {"start": v(-18.16, -72.52) * mm, "end": v(-37.21, -72.52) * mm});
            skLineSegment(sketch, "E40.2.6.3", {"start": v(-18.16, -91.57) * mm, "end": v(-18.16, -72.52) * mm});
            skLineSegment(sketch, "E40.3.0.0", {"start": v(9.27, 73.02) * mm, "end": v(-9.78, 73.02) * mm});
            skLineSegment(sketch, "E40.3.0.1", {"start": v(-9.78, 73.02) * mm, "end": v(-9.78, 92.07) * mm});
            skLineSegment(sketch, "E40.3.0.2", {"start": v(9.27, 92.07) * mm, "end": v(-9.78, 92.07) * mm});
            skLineSegment(sketch, "E40.3.0.3", {"start": v(9.27, 73.02) * mm, "end": v(9.27, 92.07) * mm});
            skLineSegment(sketch, "E40.3.1.0", {"start": v(9.27, 45.6) * mm, "end": v(-9.78, 45.6) * mm});
            skLineSegment(sketch, "E40.3.1.1", {"start": v(-9.78, 45.6) * mm, "end": v(-9.78, 64.64) * mm});
            skLineSegment(sketch, "E40.3.1.2", {"start": v(9.27, 64.64) * mm, "end": v(-9.78, 64.64) * mm});
            skLineSegment(sketch, "E40.3.1.3", {"start": v(9.27, 45.6) * mm, "end": v(9.27, 64.64) * mm});
            skLineSegment(sketch, "E40.3.2.0", {"start": v(9.27, 18.16) * mm, "end": v(-9.78, 18.16) * mm});
            skLineSegment(sketch, "E40.3.2.1", {"start": v(-9.78, 18.16) * mm, "end": v(-9.78, 37.21) * mm});
            skLineSegment(sketch, "E40.3.2.2", {"start": v(9.27, 37.21) * mm, "end": v(-9.78, 37.21) * mm});
            skLineSegment(sketch, "E40.3.2.3", {"start": v(9.27, 18.16) * mm, "end": v(9.27, 37.21) * mm});
            skLineSegment(sketch, "E40.3.3.0", {"start": v(9.27, -9.27) * mm, "end": v(-9.78, -9.27) * mm});
            skLineSegment(sketch, "E40.3.3.1", {"start": v(-9.78, -9.27) * mm, "end": v(-9.78, 9.78) * mm});
            skLineSegment(sketch, "E40.3.3.2", {"start": v(9.27, 9.78) * mm, "end": v(-9.78, 9.78) * mm});
            skLineSegment(sketch, "E40.3.3.3", {"start": v(9.27, -9.27) * mm, "end": v(9.27, 9.78) * mm});
            skLineSegment(sketch, "E40.3.4.0", {"start": v(9.27, -36.7) * mm, "end": v(-9.78, -36.7) * mm});
            skLineSegment(sketch, "E40.3.4.1", {"start": v(-9.78, -36.7) * mm, "end": v(-9.78, -17.65) * mm});
            skLineSegment(sketch, "E40.3.4.2", {"start": v(9.27, -17.65) * mm, "end": v(-9.78, -17.65) * mm});
            skLineSegment(sketch, "E40.3.4.3", {"start": v(9.27, -36.7) * mm, "end": v(9.27, -17.65) * mm});
            skLineSegment(sketch, "E40.3.5.0", {"start": v(9.27, -64.14) * mm, "end": v(-9.78, -64.14) * mm});
            skLineSegment(sketch, "E40.3.5.1", {"start": v(-9.78, -64.14) * mm, "end": v(-9.78, -45.09) * mm});
            skLineSegment(sketch, "E40.3.5.2", {"start": v(9.27, -45.09) * mm, "end": v(-9.78, -45.09) * mm});
            skLineSegment(sketch, "E40.3.5.3", {"start": v(9.27, -64.14) * mm, "end": v(9.27, -45.09) * mm});
            skLineSegment(sketch, "E40.3.6.0", {"start": v(9.27, -91.57) * mm, "end": v(-9.78, -91.57) * mm});
            skLineSegment(sketch, "E40.3.6.1", {"start": v(-9.78, -91.57) * mm, "end": v(-9.78, -72.52) * mm});
            skLineSegment(sketch, "E40.3.6.2", {"start": v(9.27, -72.52) * mm, "end": v(-9.78, -72.52) * mm});
            skLineSegment(sketch, "E40.3.6.3", {"start": v(9.27, -91.57) * mm, "end": v(9.27, -72.52) * mm});
            skLineSegment(sketch, "E40.4.0.0", {"start": v(36.7, 73.02) * mm, "end": v(17.65, 73.02) * mm});
            skLineSegment(sketch, "E40.4.0.1", {"start": v(17.65, 73.02) * mm, "end": v(17.65, 92.07) * mm});
            skLineSegment(sketch, "E40.4.0.2", {"start": v(36.7, 92.07) * mm, "end": v(17.65, 92.07) * mm});
            skLineSegment(sketch, "E40.4.0.3", {"start": v(36.7, 73.02) * mm, "end": v(36.7, 92.07) * mm});
            skLineSegment(sketch, "E40.4.1.0", {"start": v(36.7, 45.6) * mm, "end": v(17.65, 45.6) * mm});
            skLineSegment(sketch, "E40.4.1.1", {"start": v(17.65, 45.6) * mm, "end": v(17.65, 64.64) * mm});
            skLineSegment(sketch, "E40.4.1.2", {"start": v(36.7, 64.64) * mm, "end": v(17.65, 64.64) * mm});
            skLineSegment(sketch, "E40.4.1.3", {"start": v(36.7, 45.6) * mm, "end": v(36.7, 64.64) * mm});
            skLineSegment(sketch, "E40.4.2.0", {"start": v(36.7, 18.16) * mm, "end": v(17.65, 18.16) * mm});
            skLineSegment(sketch, "E40.4.2.1", {"start": v(17.65, 18.16) * mm, "end": v(17.65, 37.21) * mm});
            skLineSegment(sketch, "E40.4.2.2", {"start": v(36.7, 37.21) * mm, "end": v(17.65, 37.21) * mm});
            skLineSegment(sketch, "E40.4.2.3", {"start": v(36.7, 18.16) * mm, "end": v(36.7, 37.21) * mm});
            skLineSegment(sketch, "E40.4.3.0", {"start": v(36.7, -9.27) * mm, "end": v(17.65, -9.27) * mm});
            skLineSegment(sketch, "E40.4.3.1", {"start": v(17.65, -9.27) * mm, "end": v(17.65, 9.78) * mm});
            skLineSegment(sketch, "E40.4.3.2", {"start": v(36.7, 9.78) * mm, "end": v(17.65, 9.78) * mm});
            skLineSegment(sketch, "E40.4.3.3", {"start": v(36.7, -9.27) * mm, "end": v(36.7, 9.78) * mm});
            skLineSegment(sketch, "E40.4.4.0", {"start": v(36.7, -36.7) * mm, "end": v(17.65, -36.7) * mm});
            skLineSegment(sketch, "E40.4.4.1", {"start": v(17.65, -36.7) * mm, "end": v(17.65, -17.65) * mm});
            skLineSegment(sketch, "E40.4.4.2", {"start": v(36.7, -17.65) * mm, "end": v(17.65, -17.65) * mm});
            skLineSegment(sketch, "E40.4.4.3", {"start": v(36.7, -36.7) * mm, "end": v(36.7, -17.65) * mm});
            skLineSegment(sketch, "E40.4.5.0", {"start": v(36.7, -64.14) * mm, "end": v(17.65, -64.14) * mm});
            skLineSegment(sketch, "E40.4.5.1", {"start": v(17.65, -64.14) * mm, "end": v(17.65, -45.09) * mm});
            skLineSegment(sketch, "E40.4.5.2", {"start": v(36.7, -45.09) * mm, "end": v(17.65, -45.09) * mm});
            skLineSegment(sketch, "E40.4.5.3", {"start": v(36.7, -64.14) * mm, "end": v(36.7, -45.09) * mm});
            skLineSegment(sketch, "E40.4.6.0", {"start": v(36.7, -91.57) * mm, "end": v(17.65, -91.57) * mm});
            skLineSegment(sketch, "E40.4.6.1", {"start": v(17.65, -91.57) * mm, "end": v(17.65, -72.52) * mm});
            skLineSegment(sketch, "E40.4.6.2", {"start": v(36.7, -72.52) * mm, "end": v(17.65, -72.52) * mm});
            skLineSegment(sketch, "E40.4.6.3", {"start": v(36.7, -91.57) * mm, "end": v(36.7, -72.52) * mm});
            skLineSegment(sketch, "E40.5.0.0", {"start": v(64.14, 73.02) * mm, "end": v(45.09, 73.02) * mm});
            skLineSegment(sketch, "E40.5.0.1", {"start": v(45.09, 73.02) * mm, "end": v(45.09, 92.07) * mm});
            skLineSegment(sketch, "E40.5.0.2", {"start": v(64.13, 92.07) * mm, "end": v(45.09, 92.07) * mm});
            skLineSegment(sketch, "E40.5.0.3", {"start": v(64.13, 73.02) * mm, "end": v(64.13, 92.07) * mm});
            skLineSegment(sketch, "E40.5.1.0", {"start": v(64.14, 45.6) * mm, "end": v(45.09, 45.6) * mm});
            skLineSegment(sketch, "E40.5.1.1", {"start": v(45.09, 45.6) * mm, "end": v(45.09, 64.64) * mm});
            skLineSegment(sketch, "E40.5.1.2", {"start": v(64.13, 64.64) * mm, "end": v(45.09, 64.64) * mm});
            skLineSegment(sketch, "E40.5.1.3", {"start": v(64.13, 45.6) * mm, "end": v(64.13, 64.64) * mm});
            skLineSegment(sketch, "E40.5.2.0", {"start": v(64.14, 18.16) * mm, "end": v(45.09, 18.16) * mm});
            skLineSegment(sketch, "E40.5.2.1", {"start": v(45.09, 18.16) * mm, "end": v(45.09, 37.21) * mm});
            skLineSegment(sketch, "E40.5.2.2", {"start": v(64.13, 37.21) * mm, "end": v(45.09, 37.21) * mm});
            skLineSegment(sketch, "E40.5.2.3", {"start": v(64.13, 18.16) * mm, "end": v(64.13, 37.21) * mm});
            skLineSegment(sketch, "E40.5.3.0", {"start": v(64.14, -9.27) * mm, "end": v(45.09, -9.27) * mm});
            skLineSegment(sketch, "E40.5.3.1", {"start": v(45.09, -9.27) * mm, "end": v(45.09, 9.78) * mm});
            skLineSegment(sketch, "E40.5.3.2", {"start": v(64.13, 9.78) * mm, "end": v(45.09, 9.78) * mm});
            skLineSegment(sketch, "E40.5.3.3", {"start": v(64.13, -9.27) * mm, "end": v(64.13, 9.78) * mm});
            skLineSegment(sketch, "E40.5.4.0", {"start": v(64.14, -36.7) * mm, "end": v(45.09, -36.7) * mm});
            skLineSegment(sketch, "E40.5.4.1", {"start": v(45.09, -36.7) * mm, "end": v(45.09, -17.65) * mm});
            skLineSegment(sketch, "E40.5.4.2", {"start": v(64.13, -17.65) * mm, "end": v(45.09, -17.65) * mm});
            skLineSegment(sketch, "E40.5.4.3", {"start": v(64.13, -36.7) * mm, "end": v(64.13, -17.65) * mm});
            skLineSegment(sketch, "E40.5.5.0", {"start": v(64.14, -64.14) * mm, "end": v(45.09, -64.14) * mm});
            skLineSegment(sketch, "E40.5.5.1", {"start": v(45.09, -64.14) * mm, "end": v(45.09, -45.09) * mm});
            skLineSegment(sketch, "E40.5.5.2", {"start": v(64.13, -45.09) * mm, "end": v(45.09, -45.09) * mm});
            skLineSegment(sketch, "E40.5.5.3", {"start": v(64.13, -64.14) * mm, "end": v(64.13, -45.09) * mm});
            skLineSegment(sketch, "E40.5.6.0", {"start": v(64.14, -91.57) * mm, "end": v(45.09, -91.57) * mm});
            skLineSegment(sketch, "E40.5.6.1", {"start": v(45.09, -91.57) * mm, "end": v(45.09, -72.52) * mm});
            skLineSegment(sketch, "E40.5.6.2", {"start": v(64.13, -72.52) * mm, "end": v(45.09, -72.52) * mm});
            skLineSegment(sketch, "E40.5.6.3", {"start": v(64.13, -91.57) * mm, "end": v(64.13, -72.52) * mm});
            skLineSegment(sketch, "E40.6.0.0", {"start": v(91.57, 73.02) * mm, "end": v(72.52, 73.02) * mm});
            skLineSegment(sketch, "E40.6.0.1", {"start": v(72.52, 73.02) * mm, "end": v(72.52, 92.07) * mm});
            skLineSegment(sketch, "E40.6.0.2", {"start": v(91.57, 92.07) * mm, "end": v(72.52, 92.07) * mm});
            skLineSegment(sketch, "E40.6.0.3", {"start": v(91.57, 73.02) * mm, "end": v(91.57, 92.07) * mm});
            skLineSegment(sketch, "E40.6.1.0", {"start": v(91.57, 45.6) * mm, "end": v(72.52, 45.6) * mm});
            skLineSegment(sketch, "E40.6.1.1", {"start": v(72.52, 45.6) * mm, "end": v(72.52, 64.64) * mm});
            skLineSegment(sketch, "E40.6.1.2", {"start": v(91.57, 64.64) * mm, "end": v(72.52, 64.64) * mm});
            skLineSegment(sketch, "E40.6.1.3", {"start": v(91.57, 45.6) * mm, "end": v(91.57, 64.64) * mm});
            skLineSegment(sketch, "E40.6.2.0", {"start": v(91.57, 18.16) * mm, "end": v(72.52, 18.16) * mm});
            skLineSegment(sketch, "E40.6.2.1", {"start": v(72.52, 18.16) * mm, "end": v(72.52, 37.21) * mm});
            skLineSegment(sketch, "E40.6.2.2", {"start": v(91.57, 37.21) * mm, "end": v(72.52, 37.21) * mm});
            skLineSegment(sketch, "E40.6.2.3", {"start": v(91.57, 18.16) * mm, "end": v(91.57, 37.21) * mm});
            skLineSegment(sketch, "E40.6.3.0", {"start": v(91.57, -9.27) * mm, "end": v(72.52, -9.27) * mm});
            skLineSegment(sketch, "E40.6.3.1", {"start": v(72.52, -9.27) * mm, "end": v(72.52, 9.78) * mm});
            skLineSegment(sketch, "E40.6.3.2", {"start": v(91.57, 9.78) * mm, "end": v(72.52, 9.78) * mm});
            skLineSegment(sketch, "E40.6.3.3", {"start": v(91.57, -9.27) * mm, "end": v(91.57, 9.78) * mm});
            skLineSegment(sketch, "E40.6.4.0", {"start": v(91.57, -36.7) * mm, "end": v(72.52, -36.7) * mm});
            skLineSegment(sketch, "E40.6.4.1", {"start": v(72.52, -36.7) * mm, "end": v(72.52, -17.65) * mm});
            skLineSegment(sketch, "E40.6.4.2", {"start": v(91.57, -17.65) * mm, "end": v(72.52, -17.65) * mm});
            skLineSegment(sketch, "E40.6.4.3", {"start": v(91.57, -36.7) * mm, "end": v(91.57, -17.65) * mm});
            skLineSegment(sketch, "E40.6.5.0", {"start": v(91.57, -64.14) * mm, "end": v(72.52, -64.14) * mm});
            skLineSegment(sketch, "E40.6.5.1", {"start": v(72.52, -64.14) * mm, "end": v(72.52, -45.09) * mm});
            skLineSegment(sketch, "E40.6.5.2", {"start": v(91.57, -45.09) * mm, "end": v(72.52, -45.09) * mm});
            skLineSegment(sketch, "E40.6.5.3", {"start": v(91.57, -64.14) * mm, "end": v(91.57, -45.09) * mm});
            skLineSegment(sketch, "E40.6.6.0", {"start": v(91.57, -91.57) * mm, "end": v(72.52, -91.57) * mm});
            skLineSegment(sketch, "E40.6.6.1", {"start": v(72.52, -91.57) * mm, "end": v(72.52, -72.52) * mm});
            skLineSegment(sketch, "E40.6.6.2", {"start": v(91.57, -72.52) * mm, "end": v(72.52, -72.52) * mm});
            skLineSegment(sketch, "E40.6.6.3", {"start": v(91.57, -91.57) * mm, "end": v(91.57, -72.52) * mm});
            skLineSegment(sketch, "E40.direction1", {"start": v(-92.08, 73.02) * mm, "end": v(-64.64, 73.02) * mm, "construction": true});
            skLineSegment(sketch, "E40.direction2", {"start": v(-92.08, 73.02) * mm, "end": v(-92.08, 45.6) * mm, "construction": true});
            skSolve(sketch);
        }
        {
            var Q0;
            Q0=qSketchRegion(id+"F16",true);
            extrude(context, id + "F17", {"entities" : qUnion([Q0]), "operationType" : NewBodyOperationType.REMOVE, "endBound" : BoundingType.THROUGH_ALL, "oppositeDirection" : true, "depth" : 25.4 * mm});
        }
    });
